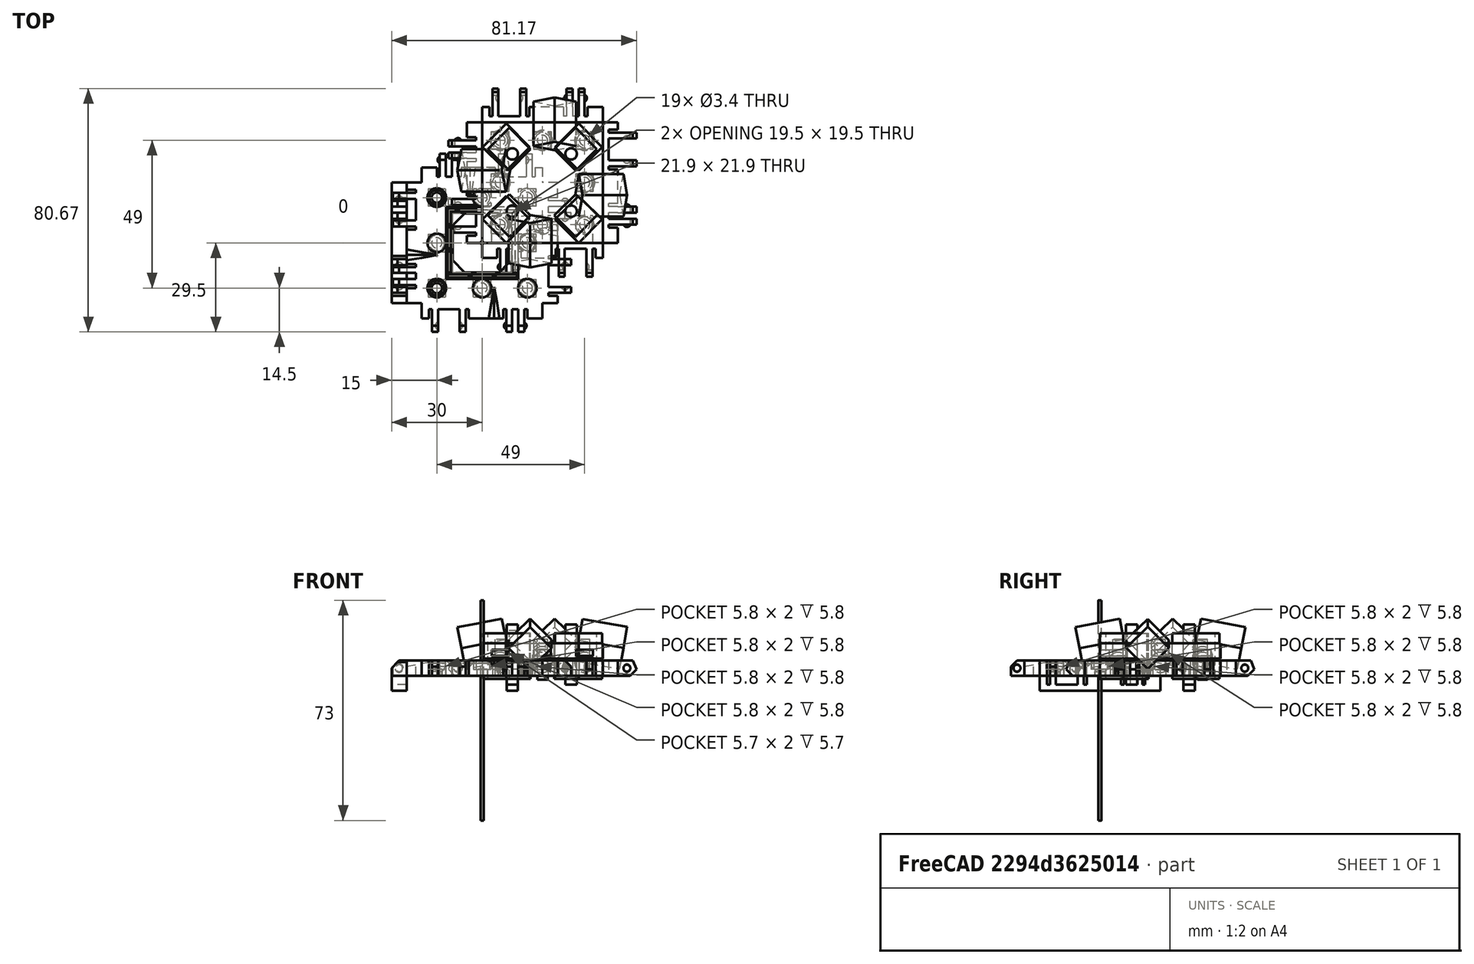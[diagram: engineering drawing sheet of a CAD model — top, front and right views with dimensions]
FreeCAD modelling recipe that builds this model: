
FCSTD DOCUMENT  (FreeCAD 0.17R13522 (Git))
Label: Robot Plates 1.0
License: All rights reserved
LicenseURL: http://en.wikipedia.org/wiki/All_rights_reserved
objects: Part::Box×265, Part::Cut×89, Part::Sphere×84, Part::MultiFuse×63, Part::Fuse×30, Part::Cylinder×29, Part::Chamfer×11, Drawing::FeatureViewAnnotation×6, App::DocumentObjectGroup×3, Part::Feature×3, Drawing::FeaturePage×2
note: 574 computed .brp shape members not serialized (recipe doc carries the construction recipe); baked Part::Feature solids carry a one-line shape summary decoded from their .brp

FEATURE [Part::Box] Box  label="Cube"
  AttacherType = Attacher::AttachEngine3D
  Height = 5
  Length = 40
  Placement = pos=(-20,-20,-2) rot=(0,0,1;0rad)
  Width = 40
FEATURE [Part::Sphere] Sphere003  label="Mag Hole 3"
  Angle1 = -90
  Angle2 = 90
  Angle3 = 360
  AttacherType = Attacher::AttachEngine3D
  Placement = pos=(-15,15,1.7) rot=(0,0,1;0rad)
  Radius = 2.85
FEATURE [Part::Sphere] Sphere005  label="Mag Hole 2"
  Angle1 = -90
  Angle2 = 90
  Angle3 = 360
  AttacherType = Attacher::AttachEngine3D
  Placement = pos=(15,0,1.7) rot=(0,0,1;0rad)
  Radius = 2.85
FEATURE [Part::Sphere] Sphere  label="Mag Hole"
  Angle1 = -90
  Angle2 = 90
  Angle3 = 360
  AttacherType = Attacher::AttachEngine3D
  Placement = pos=(-15,-15,1.7) rot=(0,0,1;0rad)
  Radius = 2.85
FEATURE [Part::MultiFuse] Fusion004  label="Ball Holes"
  Shapes = -> [Sphere,Sphere005,Sphere003]
FEATURE [Part::Cut] Cut003
  Base = -> Box
  Tool = -> Fusion004
FEATURE [Part::Box] Box001  label="Cube001"
  AttacherType = Attacher::AttachEngine3D
  Height = 7
  Length = 5
  Placement = pos=(-5,0,-2) rot=(0,0,1;0rad)
  Width = 40
FEATURE [Part::Box] Box002  label="Cube002"
  AttacherType = Attacher::AttachEngine3D
  Height = 7
  Length = 10
  Placement = pos=(-15,6,-2) rot=(0,0,1;0rad)
  Width = 2
FEATURE [Part::Box] Box003  label="Cube003"
  AttacherType = Attacher::AttachEngine3D
  Height = 7
  Length = 10
  Placement = pos=(-15,10,-2) rot=(0,0,1;0rad)
  Width = 2
FEATURE [Part::Box] Box004  label="Cube004"
  AttacherType = Attacher::AttachEngine3D
  Height = 7
  Length = 10
  Placement = pos=(-15,25.4,-2) rot=(0,0,1;0rad)
  Width = 2
FEATURE [Part::Box] Box005  label="Cube005"
  AttacherType = Attacher::AttachEngine3D
  Height = 7
  Length = 10
  Placement = pos=(-15,34.6,-2) rot=(0,0,1;0rad)
  Width = 2
FEATURE [Part::Sphere] Sphere008
  Angle1 = -90
  Angle2 = 90
  Angle3 = 360
  AttacherType = Attacher::AttachEngine3D
  Placement = pos=(-7.5,6.5,0.5) rot=(0,0,1;0rad)
  Radius = 1.25
FEATURE [Part::Box] Box006  label="Chamfer Cube"
  AttacherType = Attacher::AttachEngine3D
  Height = 10
  Length = 13
  Placement = pos=(-11.69,0,-1.19) rot=(0,-1,0;0.785398rad)
  Width = 40
FEATURE [Part::Sphere] Sphere009
  Angle1 = -90
  Angle2 = 90
  Angle3 = 360
  AttacherType = Attacher::AttachEngine3D
  Placement = pos=(-7.5,11.5,0.5) rot=(0,0,1;0rad)
  Radius = 1.25
FEATURE [Part::Sphere] Sphere010
  Angle1 = -90
  Angle2 = 90
  Angle3 = 360
  AttacherType = Attacher::AttachEngine3D
  Placement = pos=(-7.5,28,0.5) rot=(0,0,1;0rad)
  Radius = 1.5
FEATURE [Part::Sphere] Sphere011
  Angle1 = -90
  Angle2 = 90
  Angle3 = 360
  AttacherType = Attacher::AttachEngine3D
  Placement = pos=(-7.5,34,0.5) rot=(0,0,1;0rad)
  Radius = 1.5
FEATURE [Part::Box] Box007  label="Cube007"
  AttacherType = Attacher::AttachEngine3D
  Height = 7
  Length = 4
  Placement = pos=(-6,5,-2) rot=(0,0,1;0rad)
  Width = 1
FEATURE [Part::Box] Box008  label="Cube008"
  AttacherType = Attacher::AttachEngine3D
  Height = 7
  Length = 4
  Placement = pos=(-6,8,-2) rot=(0,0,1;0rad)
  Width = 2
FEATURE [Part::Box] Box009  label="Cube009"
  AttacherType = Attacher::AttachEngine3D
  Height = 7
  Length = 4
  Placement = pos=(-6,12,-2) rot=(0,0,1;0rad)
  Width = 1
FEATURE [Part::Box] Box010  label="Cube010"
  AttacherType = Attacher::AttachEngine3D
  Height = 7
  Length = 4
  Placement = pos=(-6,24.4,-2) rot=(0,0,1;0rad)
  Width = 1
FEATURE [Part::Box] Box011  label="Cube011"
  AttacherType = Attacher::AttachEngine3D
  Height = 7
  Length = 4
  Placement = pos=(-6,36.6,-2) rot=(0,0,1;0rad)
  Width = 1
FEATURE [Part::Box] Box012  label="Cube012"
  AttacherType = Attacher::AttachEngine3D
  Height = 7
  Length = 4
  Placement = pos=(-6,27.4,-2) rot=(0,0,1;0rad)
  Width = 7.2
FEATURE [Part::MultiFuse] Fusion003  label="Extra Holes for Clips"
  Shapes = -> [Box012,Box009,Box011,Box008,Box010,Box007]
FEATURE [Part::Box] Box013  label="Re-level Edge Clip Block"
  AttacherType = Attacher::AttachEngine3D
  Height = 10
  Length = 20
  Placement = pos=(-19,-2,3) rot=(0,0,1;0rad)
  Width = 44
FEATURE [Part::Box] Box014  label="Cube014"
  AttacherType = Attacher::AttachEngine3D
  Height = 7
  Length = 10
  Placement = pos=(-10,34.6,0) rot=(0,0,1;0rad)
  Width = 2
FEATURE [Part::Box] Box015  label="Cube015"
  AttacherType = Attacher::AttachEngine3D
  Height = 7
  Length = 5
  Width = 40
FEATURE [Part::Box] Box016  label="Cube016"
  AttacherType = Attacher::AttachEngine3D
  Height = 7
  Length = 10
  Placement = pos=(-10,25.4,0) rot=(0,0,1;0rad)
  Width = 2
FEATURE [Part::Box] Box017  label="Cube017"
  AttacherType = Attacher::AttachEngine3D
  Height = 7
  Length = 10
  Placement = pos=(-10,10,0) rot=(0,0,1;0rad)
  Width = 2
FEATURE [Part::Box] Box018  label="Cube018"
  AttacherType = Attacher::AttachEngine3D
  Height = 7
  Length = 10
  Placement = pos=(-10,6,0) rot=(0,0,1;0rad)
  Width = 2
FEATURE [Part::Sphere] Sphere012
  Angle1 = -90
  Angle2 = 90
  Angle3 = 360
  AttacherType = Attacher::AttachEngine3D
  Placement = pos=(-3,6.5,2.5) rot=(0,0,1;0rad)
  Radius = 1.25
FEATURE [Part::Box] Box019  label="Cube019"
  AttacherType = Attacher::AttachEngine3D
  Height = 10
  Length = 13
  Placement = pos=(-10.19,0,-1.19) rot=(0,-1,0;0.785398rad)
  Width = 40
FEATURE [Part::Sphere] Sphere013
  Angle1 = -90
  Angle2 = 90
  Angle3 = 360
  AttacherType = Attacher::AttachEngine3D
  Placement = pos=(-3,11.5,2.5) rot=(0,0,1;0rad)
  Radius = 1.25
FEATURE [Part::Sphere] Sphere014
  Angle1 = -90
  Angle2 = 90
  Angle3 = 360
  AttacherType = Attacher::AttachEngine3D
  Placement = pos=(-3,28,2.5) rot=(0,0,1;0rad)
  Radius = 1.5
FEATURE [Part::Sphere] Sphere015
  Angle1 = -90
  Angle2 = 90
  Angle3 = 360
  AttacherType = Attacher::AttachEngine3D
  Placement = pos=(-3,34,2.5) rot=(0,0,1;0rad)
  Radius = 1.5
FEATURE [Part::MultiFuse] Fusion005
  Shapes = -> [Box015,Box018,Box017,Box016,Box014]
FEATURE [Part::Cut] Cut005
  Base = -> Fusion005
  Tool = -> Box019
FEATURE [Part::MultiFuse] Fusion006
  Shapes = -> [Sphere012,Sphere013,Cut005]
FEATURE [Part::MultiFuse] Fusion007
  Shapes = -> [Sphere015,Sphere014]
FEATURE [Part::Cut] Cut006
  Base = -> Fusion006
  Tool = -> Fusion007
FEATURE [Part::Chamfer] Chamfer002
  Base = -> Cut006
  Edges = 4 edges r=4: [Edge31,Edge37,Edge43,Edge46]
FEATURE [Part::Box] Box020  label="Cube020"
  AttacherType = Attacher::AttachEngine3D
  Height = 7
  Length = 4
  Placement = pos=(-1,5,0) rot=(0,0,1;0rad)
  Width = 1
FEATURE [Part::Box] Box021  label="Cube021"
  AttacherType = Attacher::AttachEngine3D
  Height = 7
  Length = 4
  Placement = pos=(-1,8,0) rot=(0,0,1;0rad)
  Width = 2
FEATURE [Part::Box] Box022  label="Cube022"
  AttacherType = Attacher::AttachEngine3D
  Height = 7
  Length = 4
  Placement = pos=(-1,12,0) rot=(0,0,1;0rad)
  Width = 1
FEATURE [Part::Box] Box023  label="Cube023"
  AttacherType = Attacher::AttachEngine3D
  Height = 7
  Length = 4
  Placement = pos=(-1,24.4,0) rot=(0,0,1;0rad)
  Width = 1
FEATURE [Part::Box] Box024  label="Cube024"
  AttacherType = Attacher::AttachEngine3D
  Height = 7
  Length = 4
  Placement = pos=(-1,36.6,0) rot=(0,0,1;0rad)
  Width = 1
FEATURE [Part::Box] Box025  label="Cube025"
  AttacherType = Attacher::AttachEngine3D
  Height = 7
  Length = 4
  Placement = pos=(-1,27.4,0) rot=(0,0,1;0rad)
  Width = 7.2
FEATURE [Part::MultiFuse] Fusion008
  Shapes = -> [Box025,Box022,Box024,Box021,Box023,Box020]
FEATURE [Part::Cut] Cut007
  Base = -> Chamfer002
  Placement = pos=(-5,40,3) rot=(1,0,0;3.14159rad)
  Tool = -> Fusion008
FEATURE [Part::Box] Box026  label="Cube026"
  AttacherType = Attacher::AttachEngine3D
  Height = 10
  Length = 12
  Placement = pos=(-11,-2,-12) rot=(0,0,1;0rad)
  Width = 44
FEATURE [Part::Cut] Cut008
  Base = -> Cut007
  Placement = pos=(40,0,0) rot=(0,0,1;1.5708rad)
  Tool = -> Box026
FEATURE [Part::Box] Box027  label="Cube027"
  AttacherType = Attacher::AttachEngine3D
  Height = 7
  Length = 4
  Placement = pos=(-1,12,0) rot=(0,0,1;0rad)
  Width = 1
FEATURE [Part::Box] Box028  label="Cube028"
  AttacherType = Attacher::AttachEngine3D
  Height = 10
  Length = 13
  Placement = pos=(-10.19,0,-1.19) rot=(0,-1,0;0.785398rad)
  Width = 40
FEATURE [Part::Box] Box029  label="Cube029"
  AttacherType = Attacher::AttachEngine3D
  Height = 7
  Length = 4
  Placement = pos=(-1,27.4,0) rot=(0,0,1;0rad)
  Width = 7.2
FEATURE [Part::Box] Box030  label="Cube030"
  AttacherType = Attacher::AttachEngine3D
  Height = 7
  Length = 4
  Placement = pos=(-1,5,0) rot=(0,0,1;0rad)
  Width = 1
FEATURE [Part::Box] Box031  label="Cube031"
  AttacherType = Attacher::AttachEngine3D
  Height = 7
  Length = 10
  Placement = pos=(-10,6,0) rot=(0,0,1;0rad)
  Width = 2
FEATURE [Part::Box] Box032  label="Cube032"
  AttacherType = Attacher::AttachEngine3D
  Height = 10
  Length = 12
  Placement = pos=(-11,-2,-12) rot=(0,0,1;0rad)
  Width = 44
FEATURE [Part::Sphere] Sphere016
  Angle1 = -90
  Angle2 = 90
  Angle3 = 360
  AttacherType = Attacher::AttachEngine3D
  Placement = pos=(-3,6.5,2.5) rot=(0,0,1;0rad)
  Radius = 1.25
FEATURE [Part::Box] Box033  label="Cube033"
  AttacherType = Attacher::AttachEngine3D
  Height = 7
  Length = 10
  Placement = pos=(-10,25.4,0) rot=(0,0,1;0rad)
  Width = 2
FEATURE [Part::Box] Box034  label="Cube034"
  AttacherType = Attacher::AttachEngine3D
  Height = 7
  Length = 10
  Placement = pos=(-10,10,0) rot=(0,0,1;0rad)
  Width = 2
FEATURE [Part::Sphere] Sphere017
  Angle1 = -90
  Angle2 = 90
  Angle3 = 360
  AttacherType = Attacher::AttachEngine3D
  Placement = pos=(-3,28,2.5) rot=(0,0,1;0rad)
  Radius = 1.5
FEATURE [Part::Sphere] Sphere018
  Angle1 = -90
  Angle2 = 90
  Angle3 = 360
  AttacherType = Attacher::AttachEngine3D
  Placement = pos=(-3,11.5,2.5) rot=(0,0,1;0rad)
  Radius = 1.25
FEATURE [Part::Box] Box035  label="Cube035"
  AttacherType = Attacher::AttachEngine3D
  Height = 7
  Length = 4
  Placement = pos=(-1,36.6,0) rot=(0,0,1;0rad)
  Width = 1
FEATURE [Part::Sphere] Sphere019
  Angle1 = -90
  Angle2 = 90
  Angle3 = 360
  AttacherType = Attacher::AttachEngine3D
  Placement = pos=(-3,34,2.5) rot=(0,0,1;0rad)
  Radius = 1.5
FEATURE [Part::MultiFuse] Fusion011
  Shapes = -> [Sphere019,Sphere017]
FEATURE [Part::Box] Box036  label="Cube036"
  AttacherType = Attacher::AttachEngine3D
  Height = 7
  Length = 4
  Placement = pos=(-1,8,0) rot=(0,0,1;0rad)
  Width = 2
FEATURE [Part::Box] Box037  label="Cube037"
  AttacherType = Attacher::AttachEngine3D
  Height = 7
  Length = 10
  Placement = pos=(-10,34.6,0) rot=(0,0,1;0rad)
  Width = 2
FEATURE [Part::Box] Box038  label="Cube038"
  AttacherType = Attacher::AttachEngine3D
  Height = 7
  Length = 4
  Placement = pos=(-1,24.4,0) rot=(0,0,1;0rad)
  Width = 1
FEATURE [Part::MultiFuse] Fusion009
  Shapes = -> [Box029,Box027,Box035,Box036,Box038,Box030]
FEATURE [Part::Box] Box039  label="Cube039"
  AttacherType = Attacher::AttachEngine3D
  Height = 7
  Length = 5
  Width = 40
FEATURE [Part::MultiFuse] Fusion012
  Shapes = -> [Box039,Box031,Box034,Box033,Box037]
FEATURE [Part::Cut] Cut011
  Base = -> Fusion012
  Tool = -> Box028
FEATURE [Part::MultiFuse] Fusion010
  Shapes = -> [Sphere016,Sphere018,Cut011]
FEATURE [Part::Cut] Cut012
  Base = -> Fusion010
  Tool = -> Fusion011
FEATURE [Part::Chamfer] Chamfer003
  Base = -> Cut012
  Edges = 4 edges r=4: [Edge31,Edge37,Edge43,Edge46]
FEATURE [Part::Cut] Cut010
  Base = -> Chamfer003
  Placement = pos=(-5,40,3) rot=(1,0,0;3.14159rad)
  Tool = -> Fusion009
FEATURE [Part::Cut] Cut009
  Base = -> Cut010
  Placement = pos=(40,40,0) rot=(0,0,1;3.14159rad)
  Tool = -> Box032
FEATURE [Part::Sphere] Sphere020
  Angle1 = -90
  Angle2 = 90
  Angle3 = 360
  AttacherType = Attacher::AttachEngine3D
  Placement = pos=(-3,11.5,2.5) rot=(0,0,1;0rad)
  Radius = 1.25
FEATURE [Part::Box] Box040  label="Cube040"
  AttacherType = Attacher::AttachEngine3D
  Height = 7
  Length = 10
  Placement = pos=(-10,6,0) rot=(0,0,1;0rad)
  Width = 2
FEATURE [Part::Box] Box041  label="Cube041"
  AttacherType = Attacher::AttachEngine3D
  Height = 7
  Length = 4
  Placement = pos=(-1,8,0) rot=(0,0,1;0rad)
  Width = 2
FEATURE [Part::Box] Box042  label="Cube042"
  AttacherType = Attacher::AttachEngine3D
  Height = 7
  Length = 10
  Placement = pos=(-10,10,0) rot=(0,0,1;0rad)
  Width = 2
FEATURE [Part::Box] Box043  label="Cube043"
  AttacherType = Attacher::AttachEngine3D
  Height = 10
  Length = 12
  Placement = pos=(-11,-2,-12) rot=(0,0,1;0rad)
  Width = 44
FEATURE [Part::Box] Box044  label="Cube044"
  AttacherType = Attacher::AttachEngine3D
  Height = 7
  Length = 4
  Placement = pos=(-1,5,0) rot=(0,0,1;0rad)
  Width = 1
FEATURE [Part::Sphere] Sphere021
  Angle1 = -90
  Angle2 = 90
  Angle3 = 360
  AttacherType = Attacher::AttachEngine3D
  Placement = pos=(-3,28,2.5) rot=(0,0,1;0rad)
  Radius = 1.5
FEATURE [Part::Sphere] Sphere022
  Angle1 = -90
  Angle2 = 90
  Angle3 = 360
  AttacherType = Attacher::AttachEngine3D
  Placement = pos=(-3,6.5,2.5) rot=(0,0,1;0rad)
  Radius = 1.25
FEATURE [Part::Sphere] Sphere023
  Angle1 = -90
  Angle2 = 90
  Angle3 = 360
  AttacherType = Attacher::AttachEngine3D
  Placement = pos=(-3,34,2.5) rot=(0,0,1;0rad)
  Radius = 1.5
FEATURE [Part::Box] Box045  label="Cube045"
  AttacherType = Attacher::AttachEngine3D
  Height = 7
  Length = 4
  Placement = pos=(-1,12,0) rot=(0,0,1;0rad)
  Width = 1
FEATURE [Part::Box] Box046  label="Cube046"
  AttacherType = Attacher::AttachEngine3D
  Height = 7
  Length = 5
  Width = 40
FEATURE [Part::Box] Box047  label="Cube047"
  AttacherType = Attacher::AttachEngine3D
  Height = 7
  Length = 4
  Placement = pos=(-1,36.6,0) rot=(0,0,1;0rad)
  Width = 1
FEATURE [Part::Box] Box048  label="Cube048"
  AttacherType = Attacher::AttachEngine3D
  Height = 7
  Length = 4
  Placement = pos=(-1,24.4,0) rot=(0,0,1;0rad)
  Width = 1
FEATURE [Part::Box] Box049  label="Cube049"
  AttacherType = Attacher::AttachEngine3D
  Height = 7
  Length = 10
  Placement = pos=(-10,25.4,0) rot=(0,0,1;0rad)
  Width = 2
FEATURE [Part::Box] Box050  label="Cube050"
  AttacherType = Attacher::AttachEngine3D
  Height = 10
  Length = 13
  Placement = pos=(-10.19,0,-1.19) rot=(0,-1,0;0.785398rad)
  Width = 40
FEATURE [Part::Box] Box051  label="Cube051"
  AttacherType = Attacher::AttachEngine3D
  Height = 7
  Length = 10
  Placement = pos=(-10,34.6,0) rot=(0,0,1;0rad)
  Width = 2
FEATURE [Part::MultiFuse] Fusion015
  Shapes = -> [Box046,Box040,Box042,Box049,Box051]
FEATURE [Part::Cut] Cut013
  Base = -> Fusion015
  Tool = -> Box050
FEATURE [Part::MultiFuse] Fusion013
  Shapes = -> [Sphere022,Sphere020,Cut013]
FEATURE [Part::MultiFuse] Fusion016
  Shapes = -> [Sphere023,Sphere021]
FEATURE [Part::Cut] Cut014
  Base = -> Fusion013
  Tool = -> Fusion016
FEATURE [Part::Chamfer] Chamfer004
  Base = -> Cut014
  Edges = 4 edges r=4: [Edge31,Edge37,Edge43,Edge46]
FEATURE [Part::Box] Box052  label="Cube052"
  AttacherType = Attacher::AttachEngine3D
  Height = 7
  Length = 4
  Placement = pos=(-1,27.4,0) rot=(0,0,1;0rad)
  Width = 7.2
FEATURE [Part::MultiFuse] Fusion014
  Shapes = -> [Box052,Box045,Box047,Box041,Box048,Box044]
FEATURE [Part::Cut] Cut016
  Base = -> Chamfer004
  Placement = pos=(-5,40,3) rot=(1,0,0;3.14159rad)
  Tool = -> Fusion014
FEATURE [Part::Cut] Cut015
  Base = -> Cut016
  Placement = pos=(0,40,0) rot=(0,0,-1;1.5708rad)
  Tool = -> Box043
FEATURE [Part::Box] Box054  label="Cube054"
  AttacherType = Attacher::AttachEngine3D
  Height = 15
  Length = 10
  Placement = pos=(9,2,-3) rot=(0,0,1;0.785398rad)
  Width = 10
FEATURE [Part::Box] Box055  label="Cube055"
  AttacherType = Attacher::AttachEngine3D
  Height = 15
  Length = 10
  Placement = pos=(31,24,-3) rot=(0,0,1;0.785398rad)
  Width = 10
FEATURE [Part::Box] Box056  label="Cube056"
  AttacherType = Attacher::AttachEngine3D
  Height = 15
  Length = 10
  Placement = pos=(31,2,-3) rot=(0,0,1;0.785398rad)
  Width = 10
FEATURE [Part::Box] Box057  label="Cube057"
  AttacherType = Attacher::AttachEngine3D
  Height = 15
  Length = 10
  Placement = pos=(9,24,-3) rot=(0,0,1;0.785398rad)
  Width = 10
FEATURE [Part::MultiFuse] Fusion017
  Shapes = -> [Box054,Box057,Box056,Box055]
FEATURE [Part::Box] Box058  label="Cube058"
  AttacherType = Attacher::AttachEngine3D
  Height = 5
  Length = 40
  Placement = pos=(0,0,3.7) rot=(0,0,1;0rad)
  Width = 40
FEATURE [Part::Box] Box059  label="Square Nut Hole 008"
  AttacherType = Attacher::AttachEngine3D
  Height = 2
  Length = 5.6
  Placement = pos=(17.2,31.2,4.6) rot=(0,0,1;0rad)
  Width = 5.6
FEATURE [Part::Box] Box060  label="Square Nut Hole 009"
  AttacherType = Attacher::AttachEngine3D
  Height = 2
  Length = 5.6
  Placement = pos=(17.2,-0.85,4.6) rot=(0,0,1;0rad)
  Width = 10
FEATURE [Part::Box] Box061  label="Square Nut Hole 010"
  AttacherType = Attacher::AttachEngine3D
  Height = 2
  Length = 5.6
  Placement = pos=(31.2,-0.85,4.6) rot=(0,0,1;0rad)
  Width = 10
FEATURE [Part::Box] Box062  label="Square Nut Hole 011"
  AttacherType = Attacher::AttachEngine3D
  Height = 2
  Length = 5.4
  Placement = pos=(31.3,17.3,4.6) rot=(0,0,1;0rad)
  Width = 5.4
FEATURE [Part::Box] Box063  label="Square Nut Hole 012"
  AttacherType = Attacher::AttachEngine3D
  Height = 2
  Length = 5.7
  Placement = pos=(3.15,31.15,4.6) rot=(0,0,1;0rad)
  Width = 5.7
FEATURE [Part::Box] Box064  label="Square Nut Hole 013"
  AttacherType = Attacher::AttachEngine3D
  Height = 2
  Length = 5.5
  Placement = pos=(31.25,31.25,4.6) rot=(0,0,1;0rad)
  Width = 5.5
FEATURE [Part::Box] Box065  label="Square Nut Hole 014"
  AttacherType = Attacher::AttachEngine3D
  Height = 2
  Length = 5.8
  Placement = pos=(3.1,17.1,4.6) rot=(0,0,1;0rad)
  Width = 5.8
FEATURE [Part::Box] Box066  label="Square Nut Hole 015"
  AttacherType = Attacher::AttachEngine3D
  Height = 2
  Length = 5.6
  Placement = pos=(3.2,-0.85,4.6) rot=(0,0,1;0rad)
  Width = 10
FEATURE [Part::Sphere] Sphere006  label="Nut Clearence1"
  Angle1 = -90
  Angle2 = 90
  Angle3 = 360
  AttacherType = Attacher::AttachEngine3D
  Placement = pos=(6,6,2.4) rot=(0,0,1;0rad)
  Radius = 3.35
FEATURE [Part::Sphere] Sphere024
  Angle1 = -90
  Angle2 = 90
  Angle3 = 360
  AttacherType = Attacher::AttachEngine3D
  Placement = pos=(6,34,2.4) rot=(0,0,1;0rad)
  Radius = 3.35
FEATURE [Part::Sphere] Sphere007
  Angle1 = -90
  Angle2 = 90
  Angle3 = 360
  AttacherType = Attacher::AttachEngine3D
  Placement = pos=(34,20,2.4) rot=(0,0,1;0rad)
  Radius = 3.35
FEATURE [Part::Sphere] Sphere001
  Angle1 = -90
  Angle2 = 90
  Angle3 = 360
  AttacherType = Attacher::AttachEngine3D
  Placement = pos=(34,6,2.4) rot=(0,0,1;0rad)
  Radius = 3.35
FEATURE [Part::Sphere] Sphere025
  Angle1 = -90
  Angle2 = 90
  Angle3 = 360
  AttacherType = Attacher::AttachEngine3D
  Placement = pos=(20,6,2.4) rot=(0,0,1;0rad)
  Radius = 3.35
FEATURE [Part::Sphere] Sphere026
  Angle1 = -90
  Angle2 = 90
  Angle3 = 360
  AttacherType = Attacher::AttachEngine3D
  Placement = pos=(20,34,2.4) rot=(0,0,1;0rad)
  Radius = 3.35
FEATURE [Part::Sphere] Sphere004
  Angle1 = -90
  Angle2 = 90
  Angle3 = 360
  AttacherType = Attacher::AttachEngine3D
  Placement = pos=(6,20,2.4) rot=(0,0,1;0rad)
  Radius = 3.35
FEATURE [Part::Sphere] Sphere002
  Angle1 = -90
  Angle2 = 90
  Angle3 = 360
  AttacherType = Attacher::AttachEngine3D
  Placement = pos=(34,34,2.4) rot=(0,0,1;0rad)
  Radius = 3.35
FEATURE [Part::Cylinder] Cylinder
  Angle = 360
  AttacherType = Attacher::AttachEngine3D
  Height = 10
  Placement = pos=(6,6,0) rot=(0,0,1;0rad)
  Radius = 1.7
FEATURE [Part::Cylinder] Cylinder002
  Angle = 360
  AttacherType = Attacher::AttachEngine3D
  Height = 10
  Placement = pos=(34,6,0) rot=(0,0,1;0rad)
  Radius = 1.7
FEATURE [Part::Cylinder] Cylinder001
  Angle = 360
  AttacherType = Attacher::AttachEngine3D
  Height = 10
  Placement = pos=(20,6,0) rot=(0,0,1;0rad)
  Radius = 1.7
FEATURE [Part::Cylinder] Cylinder003
  Angle = 360
  AttacherType = Attacher::AttachEngine3D
  Height = 10
  Placement = pos=(34,34,0) rot=(0,0,1;0rad)
  Radius = 1.7
FEATURE [Part::Cylinder] Cylinder004
  Angle = 360
  AttacherType = Attacher::AttachEngine3D
  Height = 10
  Placement = pos=(20,34,0) rot=(0,0,1;0rad)
  Radius = 1.7
FEATURE [Part::Cylinder] Cylinder005
  Angle = 360
  AttacherType = Attacher::AttachEngine3D
  Height = 10
  Placement = pos=(6,34,0) rot=(0,0,1;0rad)
  Radius = 1.7
FEATURE [Part::Cylinder] Cylinder006
  Angle = 360
  AttacherType = Attacher::AttachEngine3D
  Height = 10
  Placement = pos=(6,20,0) rot=(0,0,1;0rad)
  Radius = 1.7
FEATURE [Part::Cylinder] Cylinder007
  Angle = 360
  AttacherType = Attacher::AttachEngine3D
  Height = 10
  Placement = pos=(34,20,0) rot=(0,0,1;0rad)
  Radius = 1.7
FEATURE [Part::MultiFuse] Fusion018
  Shapes = -> [Cylinder,Cylinder004,Cylinder007,Cylinder005,Cylinder006,Cylinder001,Cylinder002,Cylinder003]
FEATURE [Part::MultiFuse] Fusion019
  Shapes = -> [Sphere007,Sphere024,Sphere006,Sphere025,Sphere001,Sphere026,Sphere004,Sphere002]
FEATURE [Part::MultiFuse] Fusion020
  Shapes = -> [Box061,Box065,Box062,Box063,Box064,Box066,Box059,Box060]
FEATURE [Part::Cut] Cut017
  Base = -> Box058
  Tool = -> Fusion020
FEATURE [Part::Cut] Cut019
  Base = -> Cut017
  Tool = -> Fusion019
FEATURE [Part::Cut] Cut018
  Base = -> Cut019
  Tool = -> Fusion018
FEATURE [Part::Cylinder] Cylinder008
  Angle = 360
  AttacherType = Attacher::AttachEngine3D
  Height = 20
  Placement = pos=(10,10.5,-5) rot=(0,0,1;0rad)
  Radius = 1.9
FEATURE [Part::Cylinder] Cylinder009
  Angle = 360
  AttacherType = Attacher::AttachEngine3D
  Height = 20
  Placement = pos=(29.5,10.5,-5) rot=(0,0,1;0rad)
  Radius = 1.9
FEATURE [Part::Cylinder] Cylinder010
  Angle = 360
  AttacherType = Attacher::AttachEngine3D
  Height = 20
  Placement = pos=(29.5,29.5,-5) rot=(0,0,1;0rad)
  Radius = 1.9
FEATURE [Part::Cylinder] Cylinder011
  Angle = 360
  AttacherType = Attacher::AttachEngine3D
  Height = 20
  Placement = pos=(10,29.5,-7) rot=(0,0,1;0rad)
  Radius = 1.9
FEATURE [Part::MultiFuse] Fusion021  label="M2 Screw holes"
  Shapes = -> [Cylinder008,Cylinder009,Cylinder011,Cylinder010]
FEATURE [Part::Box] Box067  label="Square Nut Hole 016"
  AttacherType = Attacher::AttachEngine3D
  Height = 2
  Length = 5.8
  Placement = pos=(31.1,17.1,4.6) rot=(0,0,1;0rad)
  Width = 5.8
FEATURE [Part::Box] Box068  label="Square Nut Hole 017"
  AttacherType = Attacher::AttachEngine3D
  Height = 2
  Length = 5.8
  Placement = pos=(17.1,36.9,2.1) rot=(1,0,0;3.14159rad)
  Width = 5.8
FEATURE [Part::Box] Box069  label="Square Nut Hole 018"
  AttacherType = Attacher::AttachEngine3D
  Height = 2
  Length = 5.8
  Placement = pos=(-2.9,2.9,2.1) rot=(1,0,0;3.14159rad)
  Width = 5.8
FEATURE [Part::Box] Box070  label="Square Nut Hole 019"
  AttacherType = Attacher::AttachEngine3D
  Height = 2
  Length = 5.8
  Placement = pos=(3.1,3.1,4.6) rot=(0,0,1;0rad)
  Width = 5.8
FEATURE [Part::Box] Box071  label="Square Nut Hole 020"
  AttacherType = Attacher::AttachEngine3D
  Height = 2
  Length = 5.8
  Placement = pos=(3.1,31.1,4.6) rot=(0,0,1;0rad)
  Width = 5.8
FEATURE [Part::Box] Box072  label="Square Nut Hole 021"
  AttacherType = Attacher::AttachEngine3D
  Height = 2
  Length = 5.8
  Placement = pos=(17.1,31.1,4.6) rot=(0,0,1;0rad)
  Width = 5.8
FEATURE [Part::Box] Box073  label="Square Nut Hole 022"
  AttacherType = Attacher::AttachEngine3D
  Height = 2
  Length = 5.8
  Placement = pos=(31.1,31.1,4.6) rot=(0,0,1;0rad)
  Width = 5.8
FEATURE [Part::Box] Box074  label="Square Nut Hole 023"
  AttacherType = Attacher::AttachEngine3D
  Height = 2
  Length = 5.8
  Placement = pos=(3.1,17.1,4.6) rot=(0,0,1;0rad)
  Width = 5.8
FEATURE [Part::Cylinder] Cylinder012
  Angle = 360
  AttacherType = Attacher::AttachEngine3D
  Height = 10
  Placement = pos=(6,6,0) rot=(0,0,1;0rad)
  Radius = 1.7
FEATURE [Part::Cylinder] Cylinder013
  Angle = 360
  AttacherType = Attacher::AttachEngine3D
  Height = 10
  Placement = pos=(34,34,0) rot=(0,0,1;0rad)
  Radius = 1.7
FEATURE [Part::Cylinder] Cylinder014
  Angle = 360
  AttacherType = Attacher::AttachEngine3D
  Height = 10
  Placement = pos=(20,34,0) rot=(0,0,1;0rad)
  Radius = 1.7
FEATURE [Part::Cylinder] Cylinder015
  Angle = 360
  AttacherType = Attacher::AttachEngine3D
  Height = 10
  Placement = pos=(6,34,0) rot=(0,0,1;0rad)
  Radius = 1.7
FEATURE [Part::Cylinder] Cylinder016
  Angle = 360
  AttacherType = Attacher::AttachEngine3D
  Height = 10
  Placement = pos=(6,20,0) rot=(0,0,1;0rad)
  Radius = 1.7
FEATURE [Part::Cylinder] Cylinder017
  Angle = 360
  AttacherType = Attacher::AttachEngine3D
  Height = 10
  Placement = pos=(34,20,0) rot=(0,0,1;0rad)
  Radius = 1.7
FEATURE [Part::Cylinder] Cylinder018
  Angle = 360
  AttacherType = Attacher::AttachEngine3D
  Height = 10
  Placement = pos=(0,0,6.7) rot=(1,0,0;3.14159rad)
  Radius = 1.7
FEATURE [Part::Cylinder] Cylinder019
  Angle = 360
  AttacherType = Attacher::AttachEngine3D
  Height = 10
  Placement = pos=(20,34,6.7) rot=(1,0,0;3.14159rad)
  Radius = 1.7
FEATURE [Part::Box] Box075  label="Cube059"
  AttacherType = Attacher::AttachEngine3D
  Height = 5
  Length = 40
  Placement = pos=(-20,-20,-2) rot=(0,0,1;0rad)
  Width = 40
FEATURE [Part::Sphere] Sphere027
  Angle1 = -90
  Angle2 = 90
  Angle3 = 360
  AttacherType = Attacher::AttachEngine3D
  Placement = pos=(34,20,2.4) rot=(0,0,1;0rad)
  Radius = 3.35
FEATURE [Part::Sphere] Sphere028  label="Nut Clearence002"
  Angle1 = -90
  Angle2 = 90
  Angle3 = 360
  AttacherType = Attacher::AttachEngine3D
  Placement = pos=(6,6,2.4) rot=(0,0,1;0rad)
  Radius = 3.35
FEATURE [Part::Sphere] Sphere029
  Angle1 = -90
  Angle2 = 90
  Angle3 = 360
  AttacherType = Attacher::AttachEngine3D
  Placement = pos=(34,34,2.4) rot=(0,0,1;0rad)
  Radius = 3.35
FEATURE [Part::Sphere] Sphere030
  Angle1 = -90
  Angle2 = 90
  Angle3 = 360
  AttacherType = Attacher::AttachEngine3D
  Placement = pos=(0,0,4.3) rot=(1,0,0;3.14159rad)
  Radius = 3.35
FEATURE [Part::Sphere] Sphere031
  Angle1 = -90
  Angle2 = 90
  Angle3 = 360
  AttacherType = Attacher::AttachEngine3D
  Placement = pos=(20,34,4.3) rot=(1,0,0;3.14159rad)
  Radius = 3.35
FEATURE [Part::Sphere] Sphere032
  Angle1 = -90
  Angle2 = 90
  Angle3 = 360
  AttacherType = Attacher::AttachEngine3D
  Placement = pos=(6,34,2.4) rot=(0,0,1;0rad)
  Radius = 3.35
FEATURE [Part::Sphere] Sphere033
  Angle1 = -90
  Angle2 = 90
  Angle3 = 360
  AttacherType = Attacher::AttachEngine3D
  Placement = pos=(6,20,2.4) rot=(0,0,1;0rad)
  Radius = 3.35
FEATURE [Part::Sphere] Sphere034
  Angle1 = -90
  Angle2 = 90
  Angle3 = 360
  AttacherType = Attacher::AttachEngine3D
  Placement = pos=(20,34,2.4) rot=(0,0,1;0rad)
  Radius = 3.35
FEATURE [Part::Box] Box076  label="Cube060"
  AttacherType = Attacher::AttachEngine3D
  Height = 15
  Length = 19.5
  Placement = pos=(-9.75,-9.75,-3) rot=(0,0,1;0rad)
  Width = 19.5
FEATURE [Part::Box] Box077  label="Cube061"
  AttacherType = Attacher::AttachEngine3D
  Height = 15
  Length = 11
  Placement = pos=(8,24,-3) rot=(0,0,1;0.785398rad)
  Width = 11
FEATURE [Part::Box] Box078  label="Cube062"
  AttacherType = Attacher::AttachEngine3D
  Height = 15
  Length = 11
  Placement = pos=(8,0,-3) rot=(0,0,1;0.785398rad)
  Width = 11
FEATURE [Part::Box] Box079  label="Cube063"
  AttacherType = Attacher::AttachEngine3D
  Height = 15
  Length = 11
  Placement = pos=(32,0,-3) rot=(0,0,1;0.785398rad)
  Width = 11
FEATURE [Part::Box] Box080  label="Cube064"
  AttacherType = Attacher::AttachEngine3D
  Height = 15
  Length = 11
  Placement = pos=(32,24,-3) rot=(0,0,1;0.785398rad)
  Width = 11
FEATURE [Part::MultiFuse] Fusion022
  Shapes = -> [Box078,Box077,Box079,Box080]
FEATURE [Part::Cylinder] Cylinder020
  Angle = 360
  AttacherType = Attacher::AttachEngine3D
  Height = 20
  Placement = pos=(29.5,10.5,-5) rot=(0,0,1;0rad)
  Radius = 1.9
FEATURE [Part::Cylinder] Cylinder021
  Angle = 360
  AttacherType = Attacher::AttachEngine3D
  Height = 20
  Placement = pos=(10,29.5,-7) rot=(0,0,1;0rad)
  Radius = 1.9
FEATURE [Part::Cylinder] Cylinder022
  Angle = 360
  AttacherType = Attacher::AttachEngine3D
  Height = 20
  Placement = pos=(10,10.5,-5) rot=(0,0,1;0rad)
  Radius = 1.9
FEATURE [Part::Cylinder] Cylinder023
  Angle = 360
  AttacherType = Attacher::AttachEngine3D
  Height = 20
  Placement = pos=(29.5,29.5,-5) rot=(0,0,1;0rad)
  Radius = 1.9
FEATURE [Part::MultiFuse] Fusion023  label="M2 Screw holes001"
  Shapes = -> [Cylinder022,Cylinder020,Cylinder021,Cylinder023]
FEATURE [App::DocumentObjectGroup] Group  label="Cubes"
  Group = -> [Fusion017,Fusion022]
FEATURE [Part::Box] Box083  label="Cube067"
  AttacherType = Attacher::AttachEngine3D
  Height = 10
  Length = 24
  Placement = pos=(-12,-12,2.1) rot=(0,0,1;0rad)
  Width = 24
FEATURE [Part::Box] Box084  label="Cube068"
  AttacherType = Attacher::AttachEngine3D
  Height = 14
  Length = 20
  Placement = pos=(-10,-10,0) rot=(0,0,1;0rad)
  Width = 20
FEATURE [Part::Cut] Cut020
  Base = -> Box083
  Tool = -> Box084
FEATURE [Part::Chamfer] Chamfer007  label="Glue Channel Ball"
  Base = -> Cut020
  Edges = 8 edges r=0.95: [Edge4,Edge5,Edge14,Edge16,Edge17,Edge18,Edge19,Edge20]
FEATURE [Part::Chamfer] Chamfer008  label="Octogon Ball"
  Base = -> Box076
  Edges = 4 edges r=4: [Edge1,Edge3,Edge5,Edge7]
FEATURE [Part::Box] Box085  label="Cube069"
  AttacherType = Attacher::AttachEngine3D
  Height = 15
  Length = 19.5
  Placement = pos=(-9.75,-9.75,-13) rot=(0,0,1;0rad)
  Width = 19.5
FEATURE [Part::Box] Box086  label="Cube070"
  AttacherType = Attacher::AttachEngine3D
  Height = 10
  Length = 10
  Placement = pos=(4,-26,1) rot=(0.205904,-0.974848,-0.085288;0.803573rad)
  Width = 15
FEATURE [Part::Box] Box089  label="Cube073"
  AttacherType = Attacher::AttachEngine3D
  Height = 10
  Length = 10
  Placement = pos=(17,32.0919,9.95) rot=(-0.225436,0.969773,-0.093378;0.807337rad)
  Width = 15
FEATURE [Part::Box] Box090  label="Cube074"
  AttacherType = Attacher::AttachEngine3D
  Height = 10
  Length = 15
  Placement = pos=(30.8481,15.8,2.86019) rot=(0.974848,0.205904,-0.085288;0.803573rad)
  Width = 10
FEATURE [Part::Box] Box091  label="Cube075"
  AttacherType = Attacher::AttachEngine3D
  Height = 10
  Length = 10
  Placement = pos=(7.9081,17,9.95) rot=(-0.450607,0.280623,0.847469;1.65638rad)
  Width = 15
FEATURE [Part::Box] Box092  label="Cube076"
  AttacherType = Attacher::AttachEngine3D
  Height = 10
  Length = 10
  Placement = pos=(23,7.9081,9.95) rot=(-0.381178,-0.08861,0.920245;3.06822rad)
  Width = 15
FEATURE [Part::Box] Box093  label="Cube077"
  AttacherType = Attacher::AttachEngine3D
  Height = 7
  Length = 5
  Width = 40
FEATURE [Part::Box] Box094  label="Cube078"
  AttacherType = Attacher::AttachEngine3D
  Height = 7
  Length = 10
  Placement = pos=(-10,6,0) rot=(0,0,1;0rad)
  Width = 2
FEATURE [Part::Box] Box095  label="Cube079"
  AttacherType = Attacher::AttachEngine3D
  Height = 7
  Length = 10
  Placement = pos=(-10,10,0) rot=(0,0,1;0rad)
  Width = 2
FEATURE [Part::Box] Box096  label="Cube080"
  AttacherType = Attacher::AttachEngine3D
  Height = 7
  Length = 10
  Placement = pos=(-10,25.4,0) rot=(0,0,1;0rad)
  Width = 2
FEATURE [Part::Box] Box097  label="Cube081"
  AttacherType = Attacher::AttachEngine3D
  Height = 7
  Length = 10
  Placement = pos=(-10,34.6,0) rot=(0,0,1;0rad)
  Width = 2
FEATURE [Part::Sphere] Sphere035
  Angle1 = -90
  Angle2 = 90
  Angle3 = 360
  AttacherType = Attacher::AttachEngine3D
  Placement = pos=(-3,6.5,2.5) rot=(0,0,1;0rad)
  Radius = 1.25
FEATURE [Part::Box] Box098  label="Cube082"
  AttacherType = Attacher::AttachEngine3D
  Height = 10
  Length = 13
  Placement = pos=(-10.19,0,-1.19) rot=(0,-1,0;0.785398rad)
  Width = 40
FEATURE [Part::Sphere] Sphere036
  Angle1 = -90
  Angle2 = 90
  Angle3 = 360
  AttacherType = Attacher::AttachEngine3D
  Placement = pos=(-3,11.5,2.5) rot=(0,0,1;0rad)
  Radius = 1.25
FEATURE [Part::Sphere] Sphere037
  Angle1 = -90
  Angle2 = 90
  Angle3 = 360
  AttacherType = Attacher::AttachEngine3D
  Placement = pos=(-3,28,2.5) rot=(0,0,1;0rad)
  Radius = 1.5
FEATURE [Part::Sphere] Sphere038
  Angle1 = -90
  Angle2 = 90
  Angle3 = 360
  AttacherType = Attacher::AttachEngine3D
  Placement = pos=(-3,34,2.5) rot=(0,0,1;0rad)
  Radius = 1.5
FEATURE [Part::MultiFuse] Fusion030
  Shapes = -> [Box093,Box094,Box095,Box096,Box097]
FEATURE [Part::Cut] Cut025
  Base = -> Fusion030
  Tool = -> Box098
FEATURE [Part::MultiFuse] Fusion031
  Shapes = -> [Sphere035,Sphere036,Cut025]
FEATURE [Part::MultiFuse] Fusion032
  Shapes = -> [Sphere038,Sphere037]
FEATURE [Part::Cut] Cut026
  Base = -> Fusion031
  Tool = -> Fusion032
FEATURE [Part::Chamfer] Chamfer009
  Base = -> Cut026
  Edges = 4 edges r=4: [Edge31,Edge37,Edge43,Edge46]
FEATURE [Part::Box] Box099  label="Cube083"
  AttacherType = Attacher::AttachEngine3D
  Height = 7
  Length = 4
  Placement = pos=(-1,5,0) rot=(0,0,1;0rad)
  Width = 1
FEATURE [Part::Box] Box100  label="Cube084"
  AttacherType = Attacher::AttachEngine3D
  Height = 7
  Length = 4
  Placement = pos=(-1,8,0) rot=(0,0,1;0rad)
  Width = 2
FEATURE [Part::Box] Box101  label="Cube085"
  AttacherType = Attacher::AttachEngine3D
  Height = 7
  Length = 4
  Placement = pos=(-1,12,0) rot=(0,0,1;0rad)
  Width = 1
FEATURE [Part::Box] Box102  label="Cube086"
  AttacherType = Attacher::AttachEngine3D
  Height = 7
  Length = 4
  Placement = pos=(-1,24.4,0) rot=(0,0,1;0rad)
  Width = 1
FEATURE [Part::Box] Box103  label="Cube087"
  AttacherType = Attacher::AttachEngine3D
  Height = 7
  Length = 4
  Placement = pos=(-1,36.6,0) rot=(0,0,1;0rad)
  Width = 1
FEATURE [Part::Box] Box104  label="Cube088"
  AttacherType = Attacher::AttachEngine3D
  Height = 7
  Length = 4
  Placement = pos=(-1,27.4,0) rot=(0,0,1;0rad)
  Width = 7.2
FEATURE [Part::MultiFuse] Fusion033
  Shapes = -> [Box104,Box101,Box103,Box100,Box102,Box099]
FEATURE [Part::Cut] Cut027
  Base = -> Chamfer009
  Placement = pos=(-5,40,3) rot=(1,0,0;3.14159rad)
  Tool = -> Fusion033
FEATURE [Part::Box] Box105  label="Cube089"
  AttacherType = Attacher::AttachEngine3D
  Height = 10
  Length = 12
  Placement = pos=(-11,-2,-12) rot=(0,0,1;0rad)
  Width = 44
FEATURE [Part::Cut] Cut028
  Base = -> Cut027
  Tool = -> Box105
FEATURE [Part::Box] Box106  label="Cube090"
  AttacherType = Attacher::AttachEngine3D
  Height = 7
  Length = 10
  Placement = pos=(-10,34.6,0) rot=(0,0,1;0rad)
  Width = 2
FEATURE [Part::Box] Box107  label="Cube091"
  AttacherType = Attacher::AttachEngine3D
  Height = 7
  Length = 5
  Width = 40
FEATURE [Part::Box] Box108  label="Cube092"
  AttacherType = Attacher::AttachEngine3D
  Height = 7
  Length = 10
  Placement = pos=(-10,25.4,0) rot=(0,0,1;0rad)
  Width = 2
FEATURE [Part::Box] Box109  label="Cube093"
  AttacherType = Attacher::AttachEngine3D
  Height = 7
  Length = 10
  Placement = pos=(-10,10,0) rot=(0,0,1;0rad)
  Width = 2
FEATURE [Part::Box] Box110  label="Cube094"
  AttacherType = Attacher::AttachEngine3D
  Height = 7
  Length = 10
  Placement = pos=(-10,6,0) rot=(0,0,1;0rad)
  Width = 2
FEATURE [Part::Sphere] Sphere039
  Angle1 = -90
  Angle2 = 90
  Angle3 = 360
  AttacherType = Attacher::AttachEngine3D
  Placement = pos=(-3,6.5,2.5) rot=(0,0,1;0rad)
  Radius = 1.25
FEATURE [Part::Box] Box111  label="Cube095"
  AttacherType = Attacher::AttachEngine3D
  Height = 10
  Length = 13
  Placement = pos=(-10.19,0,-1.19) rot=(0,-1,0;0.785398rad)
  Width = 40
FEATURE [Part::Sphere] Sphere040
  Angle1 = -90
  Angle2 = 90
  Angle3 = 360
  AttacherType = Attacher::AttachEngine3D
  Placement = pos=(-3,11.5,2.5) rot=(0,0,1;0rad)
  Radius = 1.25
FEATURE [Part::Sphere] Sphere041
  Angle1 = -90
  Angle2 = 90
  Angle3 = 360
  AttacherType = Attacher::AttachEngine3D
  Placement = pos=(-3,28,2.5) rot=(0,0,1;0rad)
  Radius = 1.5
FEATURE [Part::Sphere] Sphere042
  Angle1 = -90
  Angle2 = 90
  Angle3 = 360
  AttacherType = Attacher::AttachEngine3D
  Placement = pos=(-3,34,2.5) rot=(0,0,1;0rad)
  Radius = 1.5
FEATURE [Part::MultiFuse] Fusion034
  Shapes = -> [Box107,Box110,Box109,Box108,Box106]
FEATURE [Part::Cut] Cut029
  Base = -> Fusion034
  Tool = -> Box111
FEATURE [Part::MultiFuse] Fusion035
  Shapes = -> [Sphere039,Sphere040,Cut029]
FEATURE [Part::MultiFuse] Fusion036
  Shapes = -> [Sphere042,Sphere041]
FEATURE [Part::Cut] Cut030
  Base = -> Fusion035
  Tool = -> Fusion036
FEATURE [Part::Chamfer] Chamfer010
  Base = -> Cut030
  Edges = 4 edges r=4: [Edge31,Edge37,Edge43,Edge46]
FEATURE [Part::Box] Box112  label="Cube096"
  AttacherType = Attacher::AttachEngine3D
  Height = 7
  Length = 4
  Placement = pos=(-1,5,0) rot=(0,0,1;0rad)
  Width = 1
FEATURE [Part::Box] Box113  label="Cube097"
  AttacherType = Attacher::AttachEngine3D
  Height = 7
  Length = 4
  Placement = pos=(-1,8,0) rot=(0,0,1;0rad)
  Width = 2
FEATURE [Part::Box] Box114  label="Cube098"
  AttacherType = Attacher::AttachEngine3D
  Height = 7
  Length = 4
  Placement = pos=(-1,12,0) rot=(0,0,1;0rad)
  Width = 1
FEATURE [Part::Box] Box115  label="Cube099"
  AttacherType = Attacher::AttachEngine3D
  Height = 7
  Length = 4
  Placement = pos=(-1,24.4,0) rot=(0,0,1;0rad)
  Width = 1
FEATURE [Part::Box] Box116  label="Cube100"
  AttacherType = Attacher::AttachEngine3D
  Height = 7
  Length = 4
  Placement = pos=(-1,36.6,0) rot=(0,0,1;0rad)
  Width = 1
FEATURE [Part::Box] Box117  label="Cube101"
  AttacherType = Attacher::AttachEngine3D
  Height = 7
  Length = 4
  Placement = pos=(-1,27.4,0) rot=(0,0,1;0rad)
  Width = 7.2
FEATURE [Part::MultiFuse] Fusion037
  Shapes = -> [Box117,Box114,Box116,Box113,Box115,Box112]
FEATURE [Part::Cut] Cut031
  Base = -> Chamfer010
  Placement = pos=(-5,40,3) rot=(1,0,0;3.14159rad)
  Tool = -> Fusion037
FEATURE [Part::Box] Box118  label="Cube102"
  AttacherType = Attacher::AttachEngine3D
  Height = 10
  Length = 12
  Placement = pos=(-11,-2,-12) rot=(0,0,1;0rad)
  Width = 44
FEATURE [Part::Cut] Cut032
  Base = -> Cut031
  Placement = pos=(40,0,0) rot=(0,0,1;1.5708rad)
  Tool = -> Box118
FEATURE [Part::Box] Box119  label="Cube103"
  AttacherType = Attacher::AttachEngine3D
  Height = 7
  Length = 4
  Placement = pos=(-1,12,0) rot=(0,0,1;0rad)
  Width = 1
FEATURE [Part::Box] Box120  label="Cube104"
  AttacherType = Attacher::AttachEngine3D
  Height = 10
  Length = 13
  Placement = pos=(-10.19,0,-1.19) rot=(0,-1,0;0.785398rad)
  Width = 40
FEATURE [Part::Box] Box121  label="Cube105"
  AttacherType = Attacher::AttachEngine3D
  Height = 7
  Length = 4
  Placement = pos=(-1,27.4,0) rot=(0,0,1;0rad)
  Width = 7.2
FEATURE [Part::Box] Box122  label="Cube106"
  AttacherType = Attacher::AttachEngine3D
  Height = 7
  Length = 4
  Placement = pos=(-1,5,0) rot=(0,0,1;0rad)
  Width = 1
FEATURE [Part::Box] Box123  label="Cube107"
  AttacherType = Attacher::AttachEngine3D
  Height = 7
  Length = 10
  Placement = pos=(-10,6,0) rot=(0,0,1;0rad)
  Width = 2
FEATURE [Part::Box] Box124  label="Cube108"
  AttacherType = Attacher::AttachEngine3D
  Height = 10
  Length = 12
  Placement = pos=(-11,-2,-12) rot=(0,0,1;0rad)
  Width = 44
FEATURE [Part::Sphere] Sphere043
  Angle1 = -90
  Angle2 = 90
  Angle3 = 360
  AttacherType = Attacher::AttachEngine3D
  Placement = pos=(-3,6.5,2.5) rot=(0,0,1;0rad)
  Radius = 1.25
FEATURE [Part::Box] Box125  label="Cube109"
  AttacherType = Attacher::AttachEngine3D
  Height = 7
  Length = 10
  Placement = pos=(-10,25.4,0) rot=(0,0,1;0rad)
  Width = 2
FEATURE [Part::Box] Box126  label="Cube110"
  AttacherType = Attacher::AttachEngine3D
  Height = 7
  Length = 10
  Placement = pos=(-10,10,0) rot=(0,0,1;0rad)
  Width = 2
FEATURE [Part::Sphere] Sphere044
  Angle1 = -90
  Angle2 = 90
  Angle3 = 360
  AttacherType = Attacher::AttachEngine3D
  Placement = pos=(-3,28,2.5) rot=(0,0,1;0rad)
  Radius = 1.5
FEATURE [Part::Sphere] Sphere045
  Angle1 = -90
  Angle2 = 90
  Angle3 = 360
  AttacherType = Attacher::AttachEngine3D
  Placement = pos=(-3,11.5,2.5) rot=(0,0,1;0rad)
  Radius = 1.25
FEATURE [Part::Box] Box127  label="Cube111"
  AttacherType = Attacher::AttachEngine3D
  Height = 7
  Length = 4
  Placement = pos=(-1,36.6,0) rot=(0,0,1;0rad)
  Width = 1
FEATURE [Part::Sphere] Sphere046
  Angle1 = -90
  Angle2 = 90
  Angle3 = 360
  AttacherType = Attacher::AttachEngine3D
  Placement = pos=(-3,34,2.5) rot=(0,0,1;0rad)
  Radius = 1.5
FEATURE [Part::MultiFuse] Fusion040
  Shapes = -> [Sphere046,Sphere044]
FEATURE [Part::Box] Box128  label="Cube112"
  AttacherType = Attacher::AttachEngine3D
  Height = 7
  Length = 4
  Placement = pos=(-1,8,0) rot=(0,0,1;0rad)
  Width = 2
FEATURE [Part::Box] Box129  label="Cube113"
  AttacherType = Attacher::AttachEngine3D
  Height = 7
  Length = 10
  Placement = pos=(-10,34.6,0) rot=(0,0,1;0rad)
  Width = 2
FEATURE [Part::Box] Box130  label="Cube114"
  AttacherType = Attacher::AttachEngine3D
  Height = 7
  Length = 4
  Placement = pos=(-1,24.4,0) rot=(0,0,1;0rad)
  Width = 1
FEATURE [Part::MultiFuse] Fusion038
  Shapes = -> [Box121,Box119,Box127,Box128,Box130,Box122]
FEATURE [Part::Box] Box131  label="Cube115"
  AttacherType = Attacher::AttachEngine3D
  Height = 7
  Length = 5
  Width = 40
FEATURE [Part::MultiFuse] Fusion041
  Shapes = -> [Box131,Box123,Box126,Box125,Box129]
FEATURE [Part::Cut] Cut035
  Base = -> Fusion041
  Tool = -> Box120
FEATURE [Part::MultiFuse] Fusion039
  Shapes = -> [Sphere043,Sphere045,Cut035]
FEATURE [Part::Cut] Cut036
  Base = -> Fusion039
  Tool = -> Fusion040
FEATURE [Part::Chamfer] Chamfer011
  Base = -> Cut036
  Edges = 4 edges r=4: [Edge31,Edge37,Edge43,Edge46]
FEATURE [Part::Cut] Cut034
  Base = -> Chamfer011
  Placement = pos=(-5,40,3) rot=(1,0,0;3.14159rad)
  Tool = -> Fusion038
FEATURE [Part::Cut] Cut033
  Base = -> Cut034
  Placement = pos=(40,40,0) rot=(0,0,1;3.14159rad)
  Tool = -> Box124
FEATURE [Part::Sphere] Sphere047
  Angle1 = -90
  Angle2 = 90
  Angle3 = 360
  AttacherType = Attacher::AttachEngine3D
  Placement = pos=(-3,11.5,2.5) rot=(0,0,1;0rad)
  Radius = 1.25
FEATURE [Part::Box] Box132  label="Cube116"
  AttacherType = Attacher::AttachEngine3D
  Height = 7
  Length = 10
  Placement = pos=(-10,6,0) rot=(0,0,1;0rad)
  Width = 2
FEATURE [Part::Box] Box133  label="Cube117"
  AttacherType = Attacher::AttachEngine3D
  Height = 7
  Length = 4
  Placement = pos=(-1,8,0) rot=(0,0,1;0rad)
  Width = 2
FEATURE [Part::Box] Box134  label="Cube118"
  AttacherType = Attacher::AttachEngine3D
  Height = 7
  Length = 10
  Placement = pos=(-10,10,0) rot=(0,0,1;0rad)
  Width = 2
FEATURE [Part::Box] Box135  label="Cube119"
  AttacherType = Attacher::AttachEngine3D
  Height = 10
  Length = 12
  Placement = pos=(-11,-2,-12) rot=(0,0,1;0rad)
  Width = 44
FEATURE [Part::Box] Box136  label="Cube120"
  AttacherType = Attacher::AttachEngine3D
  Height = 7
  Length = 4
  Placement = pos=(-1,5,0) rot=(0,0,1;0rad)
  Width = 1
FEATURE [Part::Sphere] Sphere048
  Angle1 = -90
  Angle2 = 90
  Angle3 = 360
  AttacherType = Attacher::AttachEngine3D
  Placement = pos=(-3,28,2.5) rot=(0,0,1;0rad)
  Radius = 1.5
FEATURE [Part::Sphere] Sphere049
  Angle1 = -90
  Angle2 = 90
  Angle3 = 360
  AttacherType = Attacher::AttachEngine3D
  Placement = pos=(-3,6.5,2.5) rot=(0,0,1;0rad)
  Radius = 1.25
FEATURE [Part::Sphere] Sphere050
  Angle1 = -90
  Angle2 = 90
  Angle3 = 360
  AttacherType = Attacher::AttachEngine3D
  Placement = pos=(-3,34,2.5) rot=(0,0,1;0rad)
  Radius = 1.5
FEATURE [Part::Box] Box137  label="Cube121"
  AttacherType = Attacher::AttachEngine3D
  Height = 7
  Length = 4
  Placement = pos=(-1,12,0) rot=(0,0,1;0rad)
  Width = 1
FEATURE [Part::Box] Box138  label="Cube122"
  AttacherType = Attacher::AttachEngine3D
  Height = 7
  Length = 5
  Width = 40
FEATURE [Part::Box] Box139  label="Cube123"
  AttacherType = Attacher::AttachEngine3D
  Height = 7
  Length = 4
  Placement = pos=(-1,36.6,0) rot=(0,0,1;0rad)
  Width = 1
FEATURE [Part::Box] Box140  label="Cube124"
  AttacherType = Attacher::AttachEngine3D
  Height = 7
  Length = 4
  Placement = pos=(-1,24.4,0) rot=(0,0,1;0rad)
  Width = 1
FEATURE [Part::Box] Box141  label="Cube125"
  AttacherType = Attacher::AttachEngine3D
  Height = 7
  Length = 10
  Placement = pos=(-10,25.4,0) rot=(0,0,1;0rad)
  Width = 2
FEATURE [Part::Box] Box142  label="Cube126"
  AttacherType = Attacher::AttachEngine3D
  Height = 10
  Length = 13
  Placement = pos=(-10.19,0,-1.19) rot=(0,-1,0;0.785398rad)
  Width = 40
FEATURE [Part::Box] Box143  label="Cube127"
  AttacherType = Attacher::AttachEngine3D
  Height = 7
  Length = 10
  Placement = pos=(-10,34.6,0) rot=(0,0,1;0rad)
  Width = 2
FEATURE [Part::MultiFuse] Fusion044
  Shapes = -> [Box138,Box132,Box134,Box141,Box143]
FEATURE [Part::Cut] Cut037
  Base = -> Fusion044
  Tool = -> Box142
FEATURE [Part::MultiFuse] Fusion042
  Shapes = -> [Sphere049,Sphere047,Cut037]
FEATURE [Part::MultiFuse] Fusion045
  Shapes = -> [Sphere050,Sphere048]
FEATURE [Part::Cut] Cut038
  Base = -> Fusion042
  Tool = -> Fusion045
FEATURE [Part::Chamfer] Chamfer012
  Base = -> Cut038
  Edges = 4 edges r=4: [Edge31,Edge37,Edge43,Edge46]
FEATURE [Part::Box] Box144  label="Cube128"
  AttacherType = Attacher::AttachEngine3D
  Height = 7
  Length = 4
  Placement = pos=(-1,27.4,0) rot=(0,0,1;0rad)
  Width = 7.2
FEATURE [Part::MultiFuse] Fusion043
  Shapes = -> [Box144,Box137,Box139,Box133,Box140,Box136]
FEATURE [Part::Cut] Cut040
  Base = -> Chamfer012
  Placement = pos=(-5,40,3) rot=(1,0,0;3.14159rad)
  Tool = -> Fusion043
FEATURE [Part::Cut] Cut039
  Base = -> Cut040
  Placement = pos=(0,40,0) rot=(0,0,-1;1.5708rad)
  Tool = -> Box135
FEATURE [Part::MultiFuse] Fusion048
  Shapes = -> [Box089,Box091,Box090,Box092]
FEATURE [Part::Box] Box145  label="Cube129"
  AttacherType = Attacher::AttachEngine3D
  Height = 15
  Length = 19.5
  Placement = pos=(-9.75,-9.75,-13) rot=(0,0,1;0rad)
  Width = 19.5
FEATURE [Part::Box] Box146  label="Cube130"
  AttacherType = Attacher::AttachEngine3D
  Height = 15
  Length = 19.5
  Placement = pos=(-9.75,-9.75,-3) rot=(0,0,1;0rad)
  Width = 19.5
FEATURE [Part::Chamfer] Chamfer013  label="Octagon"
  Base = -> Box146
  Edges = 4 edges r=4: [Edge1,Edge3,Edge5,Edge7]
FEATURE [Part::Box] Box147  label="Cube131"
  AttacherType = Attacher::AttachEngine3D
  Height = 10
  Length = 24
  Placement = pos=(-12,-12,2.1) rot=(0,0,1;0rad)
  Width = 24
FEATURE [Part::Box] Box148  label="Cube132"
  AttacherType = Attacher::AttachEngine3D
  Height = 14
  Length = 20
  Placement = pos=(-10,-10,0) rot=(0,0,1;0rad)
  Width = 20
FEATURE [Part::Cut] Cut043
  Base = -> Box147
  Tool = -> Box148
FEATURE [Part::Chamfer] Chamfer014  label="Glue Channel"
  Base = -> Cut043
  Edges = 8 edges r=0.95: [Edge4,Edge5,Edge14,Edge16,Edge17,Edge18,Edge19,Edge20]
FEATURE [Part::Cut] Cut047
  Base = -> Cut003
  Tool = -> Chamfer007
FEATURE [Part::Cylinder] Cylinder024
  Angle = 360
  AttacherType = Attacher::AttachEngine3D
  Height = 10
  Placement = pos=(-15,-15,-5) rot=(0,0,1;0rad)
  Radius = 1.7
FEATURE [Part::Cylinder] Cylinder025
  Angle = 360
  AttacherType = Attacher::AttachEngine3D
  Height = 10
  Placement = pos=(15,0,-5) rot=(0,0,1;0rad)
  Radius = 1.7
FEATURE [Part::Cylinder] Cylinder026
  Angle = 360
  AttacherType = Attacher::AttachEngine3D
  Height = 10
  Placement = pos=(-15,15,-5) rot=(0,0,1;0rad)
  Radius = 1.7
FEATURE [Part::MultiFuse] Fusion052  label="Screw Holes to remove ball mags"
  Shapes = -> [Cylinder024,Cylinder025,Cylinder026]
FEATURE [Drawing::FeatureViewAnnotation] Annotation
  Font = Sans
  Rotation = 0
  Scale = 7
  Text = 0.4Added in Holes to Mag plate for removal of magnet
  ViewResult = <g transform="translate(14,23) rotate(0)">\n<text id="Annotation"\n font-family="Sans"\n font-size="7"\n fill="#000000">\n<tspan x="0" dy="1em">0.4Added in Holes to Mag plate for removal of magnet</tspan>\n</text>\n</g>
  Visible = false
  X = 14
  Y = 23
FEATURE [Part::Box] Box149  label="Re-level Edge Clip Block001"
  AttacherType = Attacher::AttachEngine3D
  Height = 10
  Length = 12
  Placement = pos=(-21.5,-2,-7) rot=(0,0,1;0rad)
  Width = 44
FEATURE [Part::Fuse] Fusion  label="Bumps"
  Base = -> Sphere008
  Tool = -> Sphere009
FEATURE [Part::Fuse] Fusion053  label="Holes"
  Base = -> Sphere010
  Tool = -> Sphere011
FEATURE [Part::MultiFuse] Fusion054
  Shapes = -> [Box001,Box002,Box003,Box004,Box005]
FEATURE [Part::Fuse] Fusion055
  Base = -> Fusion
  Tool = -> Fusion054
FEATURE [Part::Cut] Cut
  Base = -> Fusion055
  Tool = -> Fusion053
FEATURE [Part::Cut] Cut056
  Base = -> Cut
  Tool = -> Fusion003
FEATURE [Part::Cut] Cut057
  Base = -> Cut056
  Tool = -> Box013
FEATURE [Part::Cut] Cut058
  Base = -> Cut057
  Tool = -> Box149
FEATURE [Part::Cut] Cut059  label="Edge Clips Master"
  Base = -> Cut058
  Placement = pos=(-20,-20,0) rot=(0,0,1;0rad)
  Tool = -> Box006
FEATURE [Part::Box] Box150  label="Cube133"
  AttacherType = Attacher::AttachEngine3D
  Height = 7
  Length = 5
  Placement = pos=(-5,0,-2) rot=(0,0,1;0rad)
  Width = 40
FEATURE [Part::Box] Box151  label="Cube134"
  AttacherType = Attacher::AttachEngine3D
  Height = 7
  Length = 10
  Placement = pos=(-15,6,-2) rot=(0,0,1;0rad)
  Width = 2
FEATURE [Part::Box] Box152  label="Cube135"
  AttacherType = Attacher::AttachEngine3D
  Height = 7
  Length = 10
  Placement = pos=(-15,10,-2) rot=(0,0,1;0rad)
  Width = 2
FEATURE [Part::Box] Box153  label="Cube136"
  AttacherType = Attacher::AttachEngine3D
  Height = 7
  Length = 10
  Placement = pos=(-15,25.4,-2) rot=(0,0,1;0rad)
  Width = 2
FEATURE [Part::Box] Box154  label="Cube137"
  AttacherType = Attacher::AttachEngine3D
  Height = 7
  Length = 10
  Placement = pos=(-15,34.6,-2) rot=(0,0,1;0rad)
  Width = 2
FEATURE [Part::Sphere] Sphere051
  Angle1 = -90
  Angle2 = 90
  Angle3 = 360
  AttacherType = Attacher::AttachEngine3D
  Placement = pos=(-7.5,6.5,0.5) rot=(0,0,1;0rad)
  Radius = 1.25
FEATURE [Part::Box] Box155  label="Chamfer Cube001"
  AttacherType = Attacher::AttachEngine3D
  Height = 10
  Length = 13
  Placement = pos=(-11.69,0,-1.19) rot=(0,-1,0;0.785398rad)
  Width = 40
FEATURE [Part::Sphere] Sphere052
  Angle1 = -90
  Angle2 = 90
  Angle3 = 360
  AttacherType = Attacher::AttachEngine3D
  Placement = pos=(-7.5,11.5,0.5) rot=(0,0,1;0rad)
  Radius = 1.25
FEATURE [Part::Sphere] Sphere053
  Angle1 = -90
  Angle2 = 90
  Angle3 = 360
  AttacherType = Attacher::AttachEngine3D
  Placement = pos=(-7.5,28,0.5) rot=(0,0,1;0rad)
  Radius = 1.5
FEATURE [Part::Sphere] Sphere054
  Angle1 = -90
  Angle2 = 90
  Angle3 = 360
  AttacherType = Attacher::AttachEngine3D
  Placement = pos=(-7.5,34,0.5) rot=(0,0,1;0rad)
  Radius = 1.5
FEATURE [Part::Box] Box156  label="Cube138"
  AttacherType = Attacher::AttachEngine3D
  Height = 7
  Length = 4
  Placement = pos=(-6,5,-2) rot=(0,0,1;0rad)
  Width = 1
FEATURE [Part::Box] Box157  label="Cube139"
  AttacherType = Attacher::AttachEngine3D
  Height = 7
  Length = 4
  Placement = pos=(-6,8,-2) rot=(0,0,1;0rad)
  Width = 2
FEATURE [Part::Box] Box158  label="Cube140"
  AttacherType = Attacher::AttachEngine3D
  Height = 7
  Length = 4
  Placement = pos=(-6,12,-2) rot=(0,0,1;0rad)
  Width = 1
FEATURE [Part::Box] Box159  label="Cube141"
  AttacherType = Attacher::AttachEngine3D
  Height = 7
  Length = 4
  Placement = pos=(-6,24.4,-2) rot=(0,0,1;0rad)
  Width = 1
FEATURE [Part::Box] Box160  label="Cube142"
  AttacherType = Attacher::AttachEngine3D
  Height = 7
  Length = 4
  Placement = pos=(-6,36.6,-2) rot=(0,0,1;0rad)
  Width = 1
FEATURE [Part::Box] Box161  label="Cube143"
  AttacherType = Attacher::AttachEngine3D
  Height = 7
  Length = 4
  Placement = pos=(-6,27.4,-2) rot=(0,0,1;0rad)
  Width = 7.2
FEATURE [Part::MultiFuse] Fusion056  label="Extra Holes for Clips001"
  Shapes = -> [Box161,Box158,Box160,Box157,Box159,Box156]
FEATURE [Part::Box] Box162  label="Re-level Edge Clip Block002"
  AttacherType = Attacher::AttachEngine3D
  Height = 10
  Length = 20
  Placement = pos=(-19,-2,3) rot=(0,0,1;0rad)
  Width = 44
FEATURE [Part::Box] Box163  label="Re-level Edge Clip Block003"
  AttacherType = Attacher::AttachEngine3D
  Height = 10
  Length = 12
  Placement = pos=(-21.5,-2,-7) rot=(0,0,1;0rad)
  Width = 44
FEATURE [Part::Fuse] Fusion057  label="Bumps001"
  Base = -> Sphere051
  Tool = -> Sphere052
FEATURE [Part::Fuse] Fusion058  label="Holes001"
  Base = -> Sphere053
  Tool = -> Sphere054
FEATURE [Part::MultiFuse] Fusion059
  Shapes = -> [Box150,Box151,Box152,Box153,Box154]
FEATURE [Part::Fuse] Fusion060
  Base = -> Fusion057
  Tool = -> Fusion059
FEATURE [Part::Cut] Cut060
  Base = -> Fusion060
  Tool = -> Fusion058
FEATURE [Part::Cut] Cut061
  Base = -> Cut060
  Tool = -> Fusion056
FEATURE [Part::Cut] Cut062
  Base = -> Cut061
  Tool = -> Box162
FEATURE [Part::Cut] Cut063
  Base = -> Cut062
  Tool = -> Box163
FEATURE [Part::Cut] Cut064  label="Copy Edge Clip"
  Base = -> Cut063
  Placement = pos=(-27,20,-7) rot=(0.707107,0,-0.707107;3.14159rad)
  Tool = -> Box155
FEATURE [App::DocumentObjectGroup] Group001  label="Old"
  Group = -> [Cut008,Cut009,Cut015,Cut018,Fusion021,Fusion023,Group,Cut039,Cut028,Cut032,Cut033,Fusion048]
FEATURE [Part::Box] Box164  label="Cube144"
  AttacherType = Attacher::AttachEngine3D
  Height = 7
  Length = 5
  Placement = pos=(-5,0,-2) rot=(0,0,1;0rad)
  Width = 40
FEATURE [Part::Box] Box165  label="Cube145"
  AttacherType = Attacher::AttachEngine3D
  Height = 7
  Length = 10
  Placement = pos=(-15,6,-2) rot=(0,0,1;0rad)
  Width = 2
FEATURE [Part::Box] Box166  label="Cube146"
  AttacherType = Attacher::AttachEngine3D
  Height = 7
  Length = 10
  Placement = pos=(-15,10,-2) rot=(0,0,1;0rad)
  Width = 2
FEATURE [Part::Box] Box167  label="Cube147"
  AttacherType = Attacher::AttachEngine3D
  Height = 7
  Length = 10
  Placement = pos=(-15,25.4,-2) rot=(0,0,1;0rad)
  Width = 2
FEATURE [Part::Box] Box168  label="Cube148"
  AttacherType = Attacher::AttachEngine3D
  Height = 7
  Length = 10
  Placement = pos=(-15,34.6,-2) rot=(0,0,1;0rad)
  Width = 2
FEATURE [Part::Sphere] Sphere055
  Angle1 = -90
  Angle2 = 90
  Angle3 = 360
  AttacherType = Attacher::AttachEngine3D
  Placement = pos=(-7.5,6.5,0.5) rot=(0,0,1;0rad)
  Radius = 1.25
FEATURE [Part::Box] Box169  label="Chamfer Cube002"
  AttacherType = Attacher::AttachEngine3D
  Height = 10
  Length = 13
  Placement = pos=(-11.69,0,-1.19) rot=(0,-1,0;0.785398rad)
  Width = 40
FEATURE [Part::Sphere] Sphere056
  Angle1 = -90
  Angle2 = 90
  Angle3 = 360
  AttacherType = Attacher::AttachEngine3D
  Placement = pos=(-7.5,11.5,0.5) rot=(0,0,1;0rad)
  Radius = 1.25
FEATURE [Part::Sphere] Sphere057
  Angle1 = -90
  Angle2 = 90
  Angle3 = 360
  AttacherType = Attacher::AttachEngine3D
  Placement = pos=(-7.5,28,0.5) rot=(0,0,1;0rad)
  Radius = 1.5
FEATURE [Part::Sphere] Sphere058
  Angle1 = -90
  Angle2 = 90
  Angle3 = 360
  AttacherType = Attacher::AttachEngine3D
  Placement = pos=(-7.5,34,0.5) rot=(0,0,1;0rad)
  Radius = 1.5
FEATURE [Part::Box] Box170  label="Cube149"
  AttacherType = Attacher::AttachEngine3D
  Height = 7
  Length = 4
  Placement = pos=(-6,5,-2) rot=(0,0,1;0rad)
  Width = 1
FEATURE [Part::Box] Box171  label="Cube150"
  AttacherType = Attacher::AttachEngine3D
  Height = 7
  Length = 4
  Placement = pos=(-6,8,-2) rot=(0,0,1;0rad)
  Width = 2
FEATURE [Part::Box] Box172  label="Cube151"
  AttacherType = Attacher::AttachEngine3D
  Height = 7
  Length = 4
  Placement = pos=(-6,12,-2) rot=(0,0,1;0rad)
  Width = 1
FEATURE [Part::Box] Box173  label="Cube152"
  AttacherType = Attacher::AttachEngine3D
  Height = 7
  Length = 4
  Placement = pos=(-6,24.4,-2) rot=(0,0,1;0rad)
  Width = 1
FEATURE [Part::Box] Box174  label="Cube153"
  AttacherType = Attacher::AttachEngine3D
  Height = 7
  Length = 4
  Placement = pos=(-6,36.6,-2) rot=(0,0,1;0rad)
  Width = 1
FEATURE [Part::Box] Box175  label="Cube154"
  AttacherType = Attacher::AttachEngine3D
  Height = 7
  Length = 4
  Placement = pos=(-6,27.4,-2) rot=(0,0,1;0rad)
  Width = 7.2
FEATURE [Part::MultiFuse] Fusion061  label="Extra Holes for Clips002"
  Shapes = -> [Box175,Box172,Box174,Box171,Box173,Box170]
FEATURE [Part::Box] Box176  label="Re-level Edge Clip Block004"
  AttacherType = Attacher::AttachEngine3D
  Height = 10
  Length = 20
  Placement = pos=(-19,-2,3) rot=(0,0,1;0rad)
  Width = 44
FEATURE [Part::Box] Box177  label="Re-level Edge Clip Block005"
  AttacherType = Attacher::AttachEngine3D
  Height = 10
  Length = 12
  Placement = pos=(-21.5,-2,-7) rot=(0,0,1;0rad)
  Width = 44
FEATURE [Part::Fuse] Fusion062  label="Bumps002"
  Base = -> Sphere055
  Tool = -> Sphere056
FEATURE [Part::Fuse] Fusion063  label="Holes002"
  Base = -> Sphere057
  Tool = -> Sphere058
FEATURE [Part::MultiFuse] Fusion064
  Shapes = -> [Box164,Box165,Box166,Box167,Box168]
FEATURE [Part::Fuse] Fusion065
  Base = -> Fusion062
  Tool = -> Fusion064
FEATURE [Part::Cut] Cut065
  Base = -> Fusion065
  Tool = -> Fusion063
FEATURE [Part::Cut] Cut066
  Base = -> Cut065
  Tool = -> Fusion061
FEATURE [Part::Cut] Cut067
  Base = -> Cut066
  Tool = -> Box176
FEATURE [Part::Cut] Cut068
  Base = -> Cut067
  Tool = -> Box177
FEATURE [Part::Cut] Cut069  label="Edge Clips001"
  Base = -> Cut068
  Placement = pos=(20,-20,0) rot=(0,0,1;1.5708rad)
  Tool = -> Box169
FEATURE [Part::Box] Box178  label="Cube155"
  AttacherType = Attacher::AttachEngine3D
  Height = 7
  Length = 5
  Placement = pos=(-5,0,-2) rot=(0,0,1;0rad)
  Width = 40
FEATURE [Part::Box] Box179  label="Cube156"
  AttacherType = Attacher::AttachEngine3D
  Height = 7
  Length = 10
  Placement = pos=(-15,10,-2) rot=(0,0,1;0rad)
  Width = 2
FEATURE [Part::Box] Box180  label="Re-level Edge Clip Block006"
  AttacherType = Attacher::AttachEngine3D
  Height = 10
  Length = 20
  Placement = pos=(-19,-2,3) rot=(0,0,1;0rad)
  Width = 44
FEATURE [Part::Box] Box181  label="Cube157"
  AttacherType = Attacher::AttachEngine3D
  Height = 7
  Length = 4
  Placement = pos=(-6,27.4,-2) rot=(0,0,1;0rad)
  Width = 7.2
FEATURE [Part::Box] Box182  label="Cube158"
  AttacherType = Attacher::AttachEngine3D
  Height = 7
  Length = 4
  Placement = pos=(-6,12,-2) rot=(0,0,1;0rad)
  Width = 1
FEATURE [Part::Sphere] Sphere059
  Angle1 = -90
  Angle2 = 90
  Angle3 = 360
  AttacherType = Attacher::AttachEngine3D
  Placement = pos=(-7.5,6.5,0.5) rot=(0,0,1;0rad)
  Radius = 1.25
FEATURE [Part::Box] Box183  label="Cube159"
  AttacherType = Attacher::AttachEngine3D
  Height = 7
  Length = 10
  Placement = pos=(-15,25.4,-2) rot=(0,0,1;0rad)
  Width = 2
FEATURE [Part::Box] Box184  label="Cube160"
  AttacherType = Attacher::AttachEngine3D
  Height = 7
  Length = 4
  Placement = pos=(-6,36.6,-2) rot=(0,0,1;0rad)
  Width = 1
FEATURE [Part::Sphere] Sphere060
  Angle1 = -90
  Angle2 = 90
  Angle3 = 360
  AttacherType = Attacher::AttachEngine3D
  Placement = pos=(-7.5,34,0.5) rot=(0,0,1;0rad)
  Radius = 1.5
FEATURE [Part::Box] Box185  label="Cube161"
  AttacherType = Attacher::AttachEngine3D
  Height = 7
  Length = 4
  Placement = pos=(-6,24.4,-2) rot=(0,0,1;0rad)
  Width = 1
FEATURE [Part::Box] Box186  label="Cube162"
  AttacherType = Attacher::AttachEngine3D
  Height = 7
  Length = 4
  Placement = pos=(-6,8,-2) rot=(0,0,1;0rad)
  Width = 2
FEATURE [Part::Box] Box187  label="Re-level Edge Clip Block007"
  AttacherType = Attacher::AttachEngine3D
  Height = 10
  Length = 12
  Placement = pos=(-21.5,-2,-7) rot=(0,0,1;0rad)
  Width = 44
FEATURE [Part::Sphere] Sphere061
  Angle1 = -90
  Angle2 = 90
  Angle3 = 360
  AttacherType = Attacher::AttachEngine3D
  Placement = pos=(-7.5,11.5,0.5) rot=(0,0,1;0rad)
  Radius = 1.25
FEATURE [Part::Sphere] Sphere062
  Angle1 = -90
  Angle2 = 90
  Angle3 = 360
  AttacherType = Attacher::AttachEngine3D
  Placement = pos=(-7.5,28,0.5) rot=(0,0,1;0rad)
  Radius = 1.5
FEATURE [Part::Fuse] Fusion066  label="Holes003"
  Base = -> Sphere062
  Tool = -> Sphere060
FEATURE [Part::Box] Box188  label="Cube163"
  AttacherType = Attacher::AttachEngine3D
  Height = 7
  Length = 10
  Placement = pos=(-15,34.6,-2) rot=(0,0,1;0rad)
  Width = 2
FEATURE [Part::Box] Box189  label="Cube164"
  AttacherType = Attacher::AttachEngine3D
  Height = 7
  Length = 4
  Placement = pos=(-6,5,-2) rot=(0,0,1;0rad)
  Width = 1
FEATURE [Part::MultiFuse] Fusion067  label="Extra Holes for Clips003"
  Shapes = -> [Box181,Box182,Box184,Box186,Box185,Box189]
FEATURE [Part::Box] Box190  label="Cube165"
  AttacherType = Attacher::AttachEngine3D
  Height = 7
  Length = 10
  Placement = pos=(-15,6,-2) rot=(0,0,1;0rad)
  Width = 2
FEATURE [Part::MultiFuse] Fusion069
  Shapes = -> [Box178,Box190,Box179,Box183,Box188]
FEATURE [Part::Fuse] Fusion070  label="Bumps003"
  Base = -> Sphere059
  Tool = -> Sphere061
FEATURE [Part::Fuse] Fusion068
  Base = -> Fusion070
  Tool = -> Fusion069
FEATURE [Part::Cut] Cut073
  Base = -> Fusion068
  Tool = -> Fusion066
FEATURE [Part::Cut] Cut070
  Base = -> Cut073
  Tool = -> Fusion067
FEATURE [Part::Cut] Cut071
  Base = -> Cut070
  Tool = -> Box180
FEATURE [Part::Cut] Cut072
  Base = -> Cut071
  Tool = -> Box187
FEATURE [Part::Box] Box191  label="Chamfer Cube003"
  AttacherType = Attacher::AttachEngine3D
  Height = 10
  Length = 13
  Placement = pos=(-11.69,0,-1.19) rot=(0,-1,0;0.785398rad)
  Width = 40
FEATURE [Part::Cut] Cut074  label="Edge Clips002"
  Base = -> Cut072
  Placement = pos=(20,20,0) rot=(0,0,1;3.14159rad)
  Tool = -> Box191
FEATURE [Part::Box] Box192  label="Cube166"
  AttacherType = Attacher::AttachEngine3D
  Height = 7
  Length = 10
  Placement = pos=(-15,6,-2) rot=(0,0,1;0rad)
  Width = 2
FEATURE [Part::Box] Box193  label="Chamfer Cube004"
  AttacherType = Attacher::AttachEngine3D
  Height = 10
  Length = 13
  Placement = pos=(-11.69,0,-1.19) rot=(0,-1,0;0.785398rad)
  Width = 40
FEATURE [Part::Box] Box194  label="Re-level Edge Clip Block008"
  AttacherType = Attacher::AttachEngine3D
  Height = 10
  Length = 20
  Placement = pos=(-19,-2,3) rot=(0,0,1;0rad)
  Width = 44
FEATURE [Part::Box] Box195  label="Cube167"
  AttacherType = Attacher::AttachEngine3D
  Height = 7
  Length = 10
  Placement = pos=(-15,10,-2) rot=(0,0,1;0rad)
  Width = 2
FEATURE [Part::Box] Box196  label="Cube168"
  AttacherType = Attacher::AttachEngine3D
  Height = 7
  Length = 5
  Placement = pos=(-5,0,-2) rot=(0,0,1;0rad)
  Width = 40
FEATURE [Part::Box] Box197  label="Cube169"
  AttacherType = Attacher::AttachEngine3D
  Height = 7
  Length = 4
  Placement = pos=(-6,5,-2) rot=(0,0,1;0rad)
  Width = 1
FEATURE [Part::Box] Box198  label="Cube170"
  AttacherType = Attacher::AttachEngine3D
  Height = 7
  Length = 4
  Placement = pos=(-6,12,-2) rot=(0,0,1;0rad)
  Width = 1
FEATURE [Part::Box] Box199  label="Cube171"
  AttacherType = Attacher::AttachEngine3D
  Height = 7
  Length = 4
  Placement = pos=(-6,27.4,-2) rot=(0,0,1;0rad)
  Width = 7.2
FEATURE [Part::Box] Box200  label="Cube172"
  AttacherType = Attacher::AttachEngine3D
  Height = 7
  Length = 4
  Placement = pos=(-6,24.4,-2) rot=(0,0,1;0rad)
  Width = 1
FEATURE [Part::Sphere] Sphere063
  Angle1 = -90
  Angle2 = 90
  Angle3 = 360
  AttacherType = Attacher::AttachEngine3D
  Placement = pos=(-7.5,28,0.5) rot=(0,0,1;0rad)
  Radius = 1.5
FEATURE [Part::Sphere] Sphere064
  Angle1 = -90
  Angle2 = 90
  Angle3 = 360
  AttacherType = Attacher::AttachEngine3D
  Placement = pos=(-7.5,11.5,0.5) rot=(0,0,1;0rad)
  Radius = 1.25
FEATURE [Part::Box] Box201  label="Cube173"
  AttacherType = Attacher::AttachEngine3D
  Height = 7
  Length = 4
  Placement = pos=(-6,8,-2) rot=(0,0,1;0rad)
  Width = 2
FEATURE [Part::Box] Box202  label="Cube174"
  AttacherType = Attacher::AttachEngine3D
  Height = 7
  Length = 10
  Placement = pos=(-15,25.4,-2) rot=(0,0,1;0rad)
  Width = 2
FEATURE [Part::Sphere] Sphere065
  Angle1 = -90
  Angle2 = 90
  Angle3 = 360
  AttacherType = Attacher::AttachEngine3D
  Placement = pos=(-7.5,6.5,0.5) rot=(0,0,1;0rad)
  Radius = 1.25
FEATURE [Part::Fuse] Fusion073  label="Bumps004"
  Base = -> Sphere065
  Tool = -> Sphere064
FEATURE [Part::Sphere] Sphere066
  Angle1 = -90
  Angle2 = 90
  Angle3 = 360
  AttacherType = Attacher::AttachEngine3D
  Placement = pos=(-7.5,34,0.5) rot=(0,0,1;0rad)
  Radius = 1.5
FEATURE [Part::Fuse] Fusion071  label="Holes004"
  Base = -> Sphere063
  Tool = -> Sphere066
FEATURE [Part::Box] Box203  label="Re-level Edge Clip Block009"
  AttacherType = Attacher::AttachEngine3D
  Height = 10
  Length = 12
  Placement = pos=(-21.5,-2,-7) rot=(0,0,1;0rad)
  Width = 44
FEATURE [Part::Box] Box204  label="Cube175"
  AttacherType = Attacher::AttachEngine3D
  Height = 7
  Length = 4
  Placement = pos=(-6,36.6,-2) rot=(0,0,1;0rad)
  Width = 1
FEATURE [Part::MultiFuse] Fusion074  label="Extra Holes for Clips004"
  Shapes = -> [Box199,Box198,Box204,Box201,Box200,Box197]
FEATURE [Part::Box] Box205  label="Cube176"
  AttacherType = Attacher::AttachEngine3D
  Height = 7
  Length = 10
  Placement = pos=(-15,34.6,-2) rot=(0,0,1;0rad)
  Width = 2
FEATURE [Part::MultiFuse] Fusion072
  Shapes = -> [Box196,Box192,Box195,Box202,Box205]
FEATURE [Part::Fuse] Fusion075
  Base = -> Fusion073
  Tool = -> Fusion072
FEATURE [Part::Cut] Cut075
  Base = -> Fusion075
  Tool = -> Fusion071
FEATURE [Part::Cut] Cut076
  Base = -> Cut075
  Tool = -> Fusion074
FEATURE [Part::Cut] Cut078
  Base = -> Cut076
  Tool = -> Box194
FEATURE [Part::Cut] Cut077
  Base = -> Cut078
  Tool = -> Box203
FEATURE [Part::Cut] Cut079  label="Edge Clips003"
  Base = -> Cut077
  Placement = pos=(-20,20,0) rot=(0,0,-1;1.5708rad)
  Tool = -> Box193
FEATURE [Part::MultiFuse] Fusion076  label="Edge Clips Fusion"
  Shapes = -> [Cut059,Cut069,Cut074,Cut079]
FEATURE [Part::Box] Box206  label="Cube177"
  AttacherType = Attacher::AttachEngine3D
  Height = 10
  Length = 10
  Placement = pos=(26,4,1) rot=(0.442189,-0.287968,0.849437;1.66134rad)
  Width = 15
FEATURE [Part::Box] Box207  label="Cube178"
  AttacherType = Attacher::AttachEngine3D
  Height = 10
  Length = 10
  Placement = pos=(-4,26,1) rot=(0.381439,0.080566,0.920876;3.07487rad)
  Width = 15
FEATURE [Part::Box] Box208  label="Cube179"
  AttacherType = Attacher::AttachEngine3D
  Height = 10
  Length = 10
  Placement = pos=(-26,-4,1) rot=(-0.273007,-0.419215,-0.865867;1.78566rad)
  Width = 15
FEATURE [Part::MultiFuse] Fusion078  label="Glue Dents"
  Shapes = -> [Box086,Box208,Box207,Box206]
FEATURE [Part::Box] Box209  label="Cube180"
  AttacherType = Attacher::AttachEngine3D
  Height = 7
  Length = 5
  Placement = pos=(-5,0,-2) rot=(0,0,1;0rad)
  Width = 40
FEATURE [Part::Box] Box210  label="Cube181"
  AttacherType = Attacher::AttachEngine3D
  Height = 7
  Length = 10
  Placement = pos=(-15,6,-2) rot=(0,0,1;0rad)
  Width = 2
FEATURE [Part::Box] Box211  label="Cube182"
  AttacherType = Attacher::AttachEngine3D
  Height = 7
  Length = 10
  Placement = pos=(-15,10,-2) rot=(0,0,1;0rad)
  Width = 2
FEATURE [Part::Box] Box212  label="Cube183"
  AttacherType = Attacher::AttachEngine3D
  Height = 7
  Length = 10
  Placement = pos=(-15,25.4,-2) rot=(0,0,1;0rad)
  Width = 2
FEATURE [Part::Box] Box213  label="Cube184"
  AttacherType = Attacher::AttachEngine3D
  Height = 7
  Length = 10
  Placement = pos=(-15,34.6,-2) rot=(0,0,1;0rad)
  Width = 2
FEATURE [Part::Sphere] Sphere067
  Angle1 = -90
  Angle2 = 90
  Angle3 = 360
  AttacherType = Attacher::AttachEngine3D
  Placement = pos=(-7.5,6.5,0.5) rot=(0,0,1;0rad)
  Radius = 1.25
FEATURE [Part::Box] Box214  label="Chamfer Cube005"
  AttacherType = Attacher::AttachEngine3D
  Height = 10
  Length = 13
  Placement = pos=(-11.69,0,-1.19) rot=(0,-1,0;0.785398rad)
  Width = 40
FEATURE [Part::Sphere] Sphere068
  Angle1 = -90
  Angle2 = 90
  Angle3 = 360
  AttacherType = Attacher::AttachEngine3D
  Placement = pos=(-7.5,11.5,0.5) rot=(0,0,1;0rad)
  Radius = 1.25
FEATURE [Part::Sphere] Sphere069
  Angle1 = -90
  Angle2 = 90
  Angle3 = 360
  AttacherType = Attacher::AttachEngine3D
  Placement = pos=(-7.5,28,0.5) rot=(0,0,1;0rad)
  Radius = 1.5
FEATURE [Part::Sphere] Sphere070
  Angle1 = -90
  Angle2 = 90
  Angle3 = 360
  AttacherType = Attacher::AttachEngine3D
  Placement = pos=(-7.5,34,0.5) rot=(0,0,1;0rad)
  Radius = 1.5
FEATURE [Part::Box] Box215  label="Cube185"
  AttacherType = Attacher::AttachEngine3D
  Height = 7
  Length = 4
  Placement = pos=(-6,5,-2) rot=(0,0,1;0rad)
  Width = 1
FEATURE [Part::Box] Box216  label="Cube186"
  AttacherType = Attacher::AttachEngine3D
  Height = 7
  Length = 4
  Placement = pos=(-6,8,-2) rot=(0,0,1;0rad)
  Width = 2
FEATURE [Part::Box] Box217  label="Cube187"
  AttacherType = Attacher::AttachEngine3D
  Height = 7
  Length = 4
  Placement = pos=(-6,12,-2) rot=(0,0,1;0rad)
  Width = 1
FEATURE [Part::Box] Box218  label="Cube188"
  AttacherType = Attacher::AttachEngine3D
  Height = 7
  Length = 4
  Placement = pos=(-6,24.4,-2) rot=(0,0,1;0rad)
  Width = 1
FEATURE [Part::Box] Box219  label="Cube189"
  AttacherType = Attacher::AttachEngine3D
  Height = 7
  Length = 4
  Placement = pos=(-6,36.6,-2) rot=(0,0,1;0rad)
  Width = 1
FEATURE [Part::Box] Box220  label="Cube190"
  AttacherType = Attacher::AttachEngine3D
  Height = 7
  Length = 4
  Placement = pos=(-6,27.4,-2) rot=(0,0,1;0rad)
  Width = 7.2
FEATURE [Part::MultiFuse] Fusion079  label="Extra Holes for Clips005"
  Shapes = -> [Box220,Box217,Box219,Box216,Box218,Box215]
FEATURE [Part::Box] Box221  label="Re-level Edge Clip Block010"
  AttacherType = Attacher::AttachEngine3D
  Height = 10
  Length = 20
  Placement = pos=(-19,-2,3) rot=(0,0,1;0rad)
  Width = 44
FEATURE [Part::Box] Box222  label="Re-level Edge Clip Block011"
  AttacherType = Attacher::AttachEngine3D
  Height = 10
  Length = 12
  Placement = pos=(-21.5,-2,-7) rot=(0,0,1;0rad)
  Width = 44
FEATURE [Part::Fuse] Fusion080  label="Bumps005"
  Base = -> Sphere067
  Tool = -> Sphere068
FEATURE [Part::Fuse] Fusion081  label="Holes005"
  Base = -> Sphere069
  Tool = -> Sphere070
FEATURE [Part::MultiFuse] Fusion082
  Shapes = -> [Box209,Box210,Box211,Box212,Box213]
FEATURE [Part::Fuse] Fusion083
  Base = -> Fusion080
  Tool = -> Fusion082
FEATURE [Part::Cut] Cut082
  Base = -> Fusion083
  Tool = -> Fusion081
FEATURE [Part::Cut] Cut083
  Base = -> Cut082
  Tool = -> Fusion079
FEATURE [Part::Cut] Cut084
  Base = -> Cut083
  Tool = -> Box221
FEATURE [Part::Cut] Cut085
  Base = -> Cut084
  Tool = -> Box222
FEATURE [Part::Cut] Cut086  label="Edge Clips Master001"
  Base = -> Cut085
  Placement = pos=(-20,-20,0) rot=(0,0,1;0rad)
  Tool = -> Box214
FEATURE [Part::Box] Box223  label="Cube191"
  AttacherType = Attacher::AttachEngine3D
  Height = 7
  Length = 5
  Placement = pos=(-5,0,-2) rot=(0,0,1;0rad)
  Width = 40
FEATURE [Part::Box] Box224  label="Cube192"
  AttacherType = Attacher::AttachEngine3D
  Height = 7
  Length = 4
  Placement = pos=(-6,8,-2) rot=(0,0,1;0rad)
  Width = 2
FEATURE [Part::Box] Box225  label="Chamfer Cube006"
  AttacherType = Attacher::AttachEngine3D
  Height = 10
  Length = 13
  Placement = pos=(-11.69,0,-1.19) rot=(0,-1,0;0.785398rad)
  Width = 40
FEATURE [Part::Box] Box226  label="Cube193"
  AttacherType = Attacher::AttachEngine3D
  Height = 7
  Length = 10
  Placement = pos=(-15,6,-2) rot=(0,0,1;0rad)
  Width = 2
FEATURE [Part::Sphere] Sphere071
  Angle1 = -90
  Angle2 = 90
  Angle3 = 360
  AttacherType = Attacher::AttachEngine3D
  Placement = pos=(-7.5,11.5,0.5) rot=(0,0,1;0rad)
  Radius = 1.25
FEATURE [Part::Box] Box227  label="Cube194"
  AttacherType = Attacher::AttachEngine3D
  Height = 7
  Length = 4
  Placement = pos=(-6,27.4,-2) rot=(0,0,1;0rad)
  Width = 7.2
FEATURE [Part::Box] Box228  label="Cube195"
  AttacherType = Attacher::AttachEngine3D
  Height = 7
  Length = 4
  Placement = pos=(-6,12,-2) rot=(0,0,1;0rad)
  Width = 1
FEATURE [Part::Box] Box229  label="Cube196"
  AttacherType = Attacher::AttachEngine3D
  Height = 7
  Length = 4
  Placement = pos=(-6,24.4,-2) rot=(0,0,1;0rad)
  Width = 1
FEATURE [Part::Sphere] Sphere072
  Angle1 = -90
  Angle2 = 90
  Angle3 = 360
  AttacherType = Attacher::AttachEngine3D
  Placement = pos=(-7.5,6.5,0.5) rot=(0,0,1;0rad)
  Radius = 1.25
FEATURE [Part::Box] Box230  label="Cube197"
  AttacherType = Attacher::AttachEngine3D
  Height = 7
  Length = 4
  Placement = pos=(-6,36.6,-2) rot=(0,0,1;0rad)
  Width = 1
FEATURE [Part::Box] Box231  label="Cube198"
  AttacherType = Attacher::AttachEngine3D
  Height = 7
  Length = 10
  Placement = pos=(-15,10,-2) rot=(0,0,1;0rad)
  Width = 2
FEATURE [Part::Sphere] Sphere073
  Angle1 = -90
  Angle2 = 90
  Angle3 = 360
  AttacherType = Attacher::AttachEngine3D
  Placement = pos=(-7.5,34,0.5) rot=(0,0,1;0rad)
  Radius = 1.5
FEATURE [Part::Box] Box232  label="Cube199"
  AttacherType = Attacher::AttachEngine3D
  Height = 7
  Length = 4
  Placement = pos=(-6,5,-2) rot=(0,0,1;0rad)
  Width = 1
FEATURE [Part::MultiFuse] Fusion085  label="Extra Holes for Clips006"
  Shapes = -> [Box227,Box228,Box230,Box224,Box229,Box232]
FEATURE [Part::Box] Box233  label="Re-level Edge Clip Block012"
  AttacherType = Attacher::AttachEngine3D
  Height = 10
  Length = 20
  Placement = pos=(-19,-2,3) rot=(0,0,1;0rad)
  Width = 44
FEATURE [Part::Box] Box234  label="Cube200"
  AttacherType = Attacher::AttachEngine3D
  Height = 7
  Length = 10
  Placement = pos=(-15,34.6,-2) rot=(0,0,1;0rad)
  Width = 2
FEATURE [Part::Box] Box235  label="Cube201"
  AttacherType = Attacher::AttachEngine3D
  Height = 7
  Length = 10
  Placement = pos=(-15,25.4,-2) rot=(0,0,1;0rad)
  Width = 2
FEATURE [Part::MultiFuse] Fusion086
  Shapes = -> [Box223,Box226,Box231,Box235,Box234]
FEATURE [Part::Fuse] Fusion087  label="Bumps006"
  Base = -> Sphere072
  Tool = -> Sphere071
FEATURE [Part::Fuse] Fusion084
  Base = -> Fusion087
  Tool = -> Fusion086
FEATURE [Part::Sphere] Sphere074
  Angle1 = -90
  Angle2 = 90
  Angle3 = 360
  AttacherType = Attacher::AttachEngine3D
  Placement = pos=(-7.5,28,0.5) rot=(0,0,1;0rad)
  Radius = 1.5
FEATURE [Part::Fuse] Fusion088  label="Holes006"
  Base = -> Sphere074
  Tool = -> Sphere073
FEATURE [Part::Box] Box236  label="Re-level Edge Clip Block013"
  AttacherType = Attacher::AttachEngine3D
  Height = 10
  Length = 12
  Placement = pos=(-21.5,-2,-7) rot=(0,0,1;0rad)
  Width = 44
FEATURE [Part::Cut] Cut087
  Base = -> Fusion084
  Tool = -> Fusion088
FEATURE [Part::Cut] Cut088
  Base = -> Cut087
  Tool = -> Fusion085
FEATURE [Part::Cut] Cut089
  Base = -> Cut088
  Tool = -> Box233
FEATURE [Part::Cut] Cut090
  Base = -> Cut089
  Tool = -> Box236
FEATURE [Part::Cut] Cut091  label="Edge Clips004"
  Base = -> Cut090
  Placement = pos=(20,-20,0) rot=(0,0,1;1.5708rad)
  Tool = -> Box225
FEATURE [Part::Box] Box237  label="Re-level Edge Clip Block014"
  AttacherType = Attacher::AttachEngine3D
  Height = 10
  Length = 12
  Placement = pos=(-21.5,-2,-7) rot=(0,0,1;0rad)
  Width = 44
FEATURE [Part::Box] Box238  label="Cube202"
  AttacherType = Attacher::AttachEngine3D
  Height = 7
  Length = 4
  Placement = pos=(-6,36.6,-2) rot=(0,0,1;0rad)
  Width = 1
FEATURE [Part::Box] Box239  label="Cube203"
  AttacherType = Attacher::AttachEngine3D
  Height = 7
  Length = 10
  Placement = pos=(-15,10,-2) rot=(0,0,1;0rad)
  Width = 2
FEATURE [Part::Box] Box240  label="Cube204"
  AttacherType = Attacher::AttachEngine3D
  Height = 7
  Length = 10
  Placement = pos=(-15,25.4,-2) rot=(0,0,1;0rad)
  Width = 2
FEATURE [Part::Box] Box241  label="Re-level Edge Clip Block015"
  AttacherType = Attacher::AttachEngine3D
  Height = 10
  Length = 20
  Placement = pos=(-19,-2,3) rot=(0,0,1;0rad)
  Width = 44
FEATURE [Part::Box] Box242  label="Cube205"
  AttacherType = Attacher::AttachEngine3D
  Height = 7
  Length = 10
  Placement = pos=(-15,34.6,-2) rot=(0,0,1;0rad)
  Width = 2
FEATURE [Part::Sphere] Sphere075
  Angle1 = -90
  Angle2 = 90
  Angle3 = 360
  AttacherType = Attacher::AttachEngine3D
  Placement = pos=(-7.5,34,0.5) rot=(0,0,1;0rad)
  Radius = 1.5
FEATURE [Part::Sphere] Sphere076
  Angle1 = -90
  Angle2 = 90
  Angle3 = 360
  AttacherType = Attacher::AttachEngine3D
  Placement = pos=(-7.5,28,0.5) rot=(0,0,1;0rad)
  Radius = 1.5
FEATURE [Part::Fuse] Fusion089  label="Holes007"
  Base = -> Sphere076
  Tool = -> Sphere075
FEATURE [Part::Box] Box243  label="Cube206"
  AttacherType = Attacher::AttachEngine3D
  Height = 7
  Length = 4
  Placement = pos=(-6,5,-2) rot=(0,0,1;0rad)
  Width = 1
FEATURE [Part::Box] Box244  label="Cube207"
  AttacherType = Attacher::AttachEngine3D
  Height = 7
  Length = 4
  Placement = pos=(-6,24.4,-2) rot=(0,0,1;0rad)
  Width = 1
FEATURE [Part::Sphere] Sphere077
  Angle1 = -90
  Angle2 = 90
  Angle3 = 360
  AttacherType = Attacher::AttachEngine3D
  Placement = pos=(-7.5,11.5,0.5) rot=(0,0,1;0rad)
  Radius = 1.25
FEATURE [Part::Box] Box245  label="Cube208"
  AttacherType = Attacher::AttachEngine3D
  Height = 7
  Length = 4
  Placement = pos=(-6,12,-2) rot=(0,0,1;0rad)
  Width = 1
FEATURE [Part::Box] Box246  label="Chamfer Cube007"
  AttacherType = Attacher::AttachEngine3D
  Height = 10
  Length = 13
  Placement = pos=(-11.69,0,-1.19) rot=(0,-1,0;0.785398rad)
  Width = 40
FEATURE [Part::Sphere] Sphere078
  Angle1 = -90
  Angle2 = 90
  Angle3 = 360
  AttacherType = Attacher::AttachEngine3D
  Placement = pos=(-7.5,6.5,0.5) rot=(0,0,1;0rad)
  Radius = 1.25
FEATURE [Part::Fuse] Fusion090  label="Bumps007"
  Base = -> Sphere078
  Tool = -> Sphere077
FEATURE [Part::Box] Box247  label="Cube209"
  AttacherType = Attacher::AttachEngine3D
  Height = 7
  Length = 5
  Placement = pos=(-5,0,-2) rot=(0,0,1;0rad)
  Width = 40
FEATURE [Part::Box] Box248  label="Cube210"
  AttacherType = Attacher::AttachEngine3D
  Height = 7
  Length = 4
  Placement = pos=(-6,27.4,-2) rot=(0,0,1;0rad)
  Width = 7.2
FEATURE [Part::Box] Box249  label="Cube211"
  AttacherType = Attacher::AttachEngine3D
  Height = 7
  Length = 4
  Placement = pos=(-6,8,-2) rot=(0,0,1;0rad)
  Width = 2
FEATURE [Part::MultiFuse] Fusion091  label="Extra Holes for Clips007"
  Shapes = -> [Box248,Box245,Box238,Box249,Box244,Box243]
FEATURE [Part::Box] Box250  label="Cube212"
  AttacherType = Attacher::AttachEngine3D
  Height = 7
  Length = 10
  Placement = pos=(-15,6,-2) rot=(0,0,1;0rad)
  Width = 2
FEATURE [Part::MultiFuse] Fusion092
  Shapes = -> [Box247,Box250,Box239,Box240,Box242]
FEATURE [Part::Fuse] Fusion093
  Base = -> Fusion090
  Tool = -> Fusion092
FEATURE [Part::Cut] Cut093
  Base = -> Fusion093
  Tool = -> Fusion089
FEATURE [Part::Cut] Cut094
  Base = -> Cut093
  Tool = -> Fusion091
FEATURE [Part::Cut] Cut095
  Base = -> Cut094
  Tool = -> Box241
FEATURE [Part::Cut] Cut096
  Base = -> Cut095
  Tool = -> Box237
FEATURE [Part::Cut] Cut092  label="Edge Clips005"
  Base = -> Cut096
  Placement = pos=(20,20,0) rot=(0,0,1;3.14159rad)
  Tool = -> Box246
FEATURE [Part::Box] Box251  label="Re-level Edge Clip Block016"
  AttacherType = Attacher::AttachEngine3D
  Height = 10
  Length = 12
  Placement = pos=(-21.5,-2,-7) rot=(0,0,1;0rad)
  Width = 44
FEATURE [Part::Box] Box252  label="Cube213"
  AttacherType = Attacher::AttachEngine3D
  Height = 7
  Length = 10
  Placement = pos=(-15,10,-2) rot=(0,0,1;0rad)
  Width = 2
FEATURE [Part::Box] Box253  label="Cube214"
  AttacherType = Attacher::AttachEngine3D
  Height = 7
  Length = 4
  Placement = pos=(-6,12,-2) rot=(0,0,1;0rad)
  Width = 1
FEATURE [Part::Box] Box254  label="Chamfer Cube008"
  AttacherType = Attacher::AttachEngine3D
  Height = 10
  Length = 13
  Placement = pos=(-11.69,0,-1.19) rot=(0,-1,0;0.785398rad)
  Width = 40
FEATURE [Part::Sphere] Sphere079
  Angle1 = -90
  Angle2 = 90
  Angle3 = 360
  AttacherType = Attacher::AttachEngine3D
  Placement = pos=(-7.5,6.5,0.5) rot=(0,0,1;0rad)
  Radius = 1.25
FEATURE [Part::Box] Box255  label="Cube215"
  AttacherType = Attacher::AttachEngine3D
  Height = 7
  Length = 5
  Placement = pos=(-5,0,-2) rot=(0,0,1;0rad)
  Width = 40
FEATURE [Part::Box] Box256  label="Cube216"
  AttacherType = Attacher::AttachEngine3D
  Height = 7
  Length = 4
  Placement = pos=(-6,27.4,-2) rot=(0,0,1;0rad)
  Width = 7.2
FEATURE [Part::Box] Box257  label="Cube217"
  AttacherType = Attacher::AttachEngine3D
  Height = 7
  Length = 4
  Placement = pos=(-6,8,-2) rot=(0,0,1;0rad)
  Width = 2
FEATURE [Part::Box] Box258  label="Cube218"
  AttacherType = Attacher::AttachEngine3D
  Height = 7
  Length = 10
  Placement = pos=(-15,6,-2) rot=(0,0,1;0rad)
  Width = 2
FEATURE [Part::Sphere] Sphere080
  Angle1 = -90
  Angle2 = 90
  Angle3 = 360
  AttacherType = Attacher::AttachEngine3D
  Placement = pos=(-7.5,28,0.5) rot=(0,0,1;0rad)
  Radius = 1.5
FEATURE [Part::Box] Box259  label="Cube219"
  AttacherType = Attacher::AttachEngine3D
  Height = 7
  Length = 4
  Placement = pos=(-6,5,-2) rot=(0,0,1;0rad)
  Width = 1
FEATURE [Part::Box] Box260  label="Cube220"
  AttacherType = Attacher::AttachEngine3D
  Height = 7
  Length = 4
  Placement = pos=(-6,24.4,-2) rot=(0,0,1;0rad)
  Width = 1
FEATURE [Part::Sphere] Sphere081
  Angle1 = -90
  Angle2 = 90
  Angle3 = 360
  AttacherType = Attacher::AttachEngine3D
  Placement = pos=(-7.5,11.5,0.5) rot=(0,0,1;0rad)
  Radius = 1.25
FEATURE [Part::Box] Box261  label="Re-level Edge Clip Block017"
  AttacherType = Attacher::AttachEngine3D
  Height = 10
  Length = 20
  Placement = pos=(-19,-2,3) rot=(0,0,1;0rad)
  Width = 44
FEATURE [Part::Box] Box262  label="Cube221"
  AttacherType = Attacher::AttachEngine3D
  Height = 7
  Length = 10
  Placement = pos=(-15,34.6,-2) rot=(0,0,1;0rad)
  Width = 2
FEATURE [Part::Box] Box263  label="Cube222"
  AttacherType = Attacher::AttachEngine3D
  Height = 7
  Length = 10
  Placement = pos=(-15,25.4,-2) rot=(0,0,1;0rad)
  Width = 2
FEATURE [Part::MultiFuse] Fusion096
  Shapes = -> [Box255,Box258,Box252,Box263,Box262]
FEATURE [Part::Box] Box264  label="Cube223"
  AttacherType = Attacher::AttachEngine3D
  Height = 7
  Length = 4
  Placement = pos=(-6,36.6,-2) rot=(0,0,1;0rad)
  Width = 1
FEATURE [Part::MultiFuse] Fusion095  label="Extra Holes for Clips008"
  Shapes = -> [Box256,Box253,Box264,Box257,Box260,Box259]
FEATURE [Part::Fuse] Fusion098  label="Bumps008"
  Base = -> Sphere079
  Tool = -> Sphere081
FEATURE [Part::Fuse] Fusion094
  Base = -> Fusion098
  Tool = -> Fusion096
FEATURE [Part::Sphere] Sphere082
  Angle1 = -90
  Angle2 = 90
  Angle3 = 360
  AttacherType = Attacher::AttachEngine3D
  Placement = pos=(-7.5,34,0.5) rot=(0,0,1;0rad)
  Radius = 1.5
FEATURE [Part::Fuse] Fusion097  label="Holes008"
  Base = -> Sphere080
  Tool = -> Sphere082
FEATURE [Part::Cut] Cut101
  Base = -> Fusion094
  Tool = -> Fusion097
FEATURE [Part::Cut] Cut097
  Base = -> Cut101
  Tool = -> Fusion095
FEATURE [Part::Cut] Cut098
  Base = -> Cut097
  Tool = -> Box261
FEATURE [Part::Cut] Cut099
  Base = -> Cut098
  Tool = -> Box251
FEATURE [Part::Cut] Cut100  label="Edge Clips006"
  Base = -> Cut099
  Placement = pos=(-20,20,0) rot=(0,0,-1;1.5708rad)
  Tool = -> Box254
FEATURE [Part::Box] Box265  label="Cube224"
  AttacherType = Attacher::AttachEngine3D
  Height = 10
  Length = 10
  Placement = pos=(4,-26,1) rot=(0.205904,-0.974848,-0.085288;0.803573rad)
  Width = 15
FEATURE [Part::Box] Box266  label="Cube225"
  AttacherType = Attacher::AttachEngine3D
  Height = 10
  Length = 10
  Placement = pos=(-26,-4,1) rot=(-0.273007,-0.419215,-0.865867;1.78566rad)
  Width = 15
FEATURE [Part::Box] Box267  label="Cube226"
  AttacherType = Attacher::AttachEngine3D
  Height = 10
  Length = 10
  Placement = pos=(-4,26,1) rot=(0.381439,0.080566,0.920876;3.07487rad)
  Width = 15
FEATURE [Part::Box] Box268  label="Cube227"
  AttacherType = Attacher::AttachEngine3D
  Height = 10
  Length = 10
  Placement = pos=(26,4,1) rot=(0.442189,-0.287968,0.849437;1.66134rad)
  Width = 15
FEATURE [Part::MultiFuse] Fusion099  label="Glue Dents001"
  Shapes = -> [Box265,Box266,Box267,Box268]
FEATURE [Part::MultiFuse] Fusion100  label="Edge Clips Fusion001"
  Shapes = -> [Cut100,Cut086,Cut091,Cut092]
FEATURE [Drawing::FeatureViewAnnotation] Annotation001
  Font = Sans
  Rotation = 0
  Scale = 7
  Text = 0.5 rejigged whole thing, stopped clips overhang and moved bump and holes back 0.5
  ViewResult = <g transform="translate(14,30) rotate(0)">\n<text id="Annotation001"\n font-family="Sans"\n font-size="7"\n fill="#000000">\n<tspan x="0" dy="1em">0.5 rejigged whole thing, stopped clips overhang and moved bump and holes back 0.5</tspan>\n</text>\n</g>
  Visible = false
  X = 14
  Y = 30
FEATURE [Part::Cylinder] Cylinder027
  Angle = 360
  AttacherType = Attacher::AttachEngine3D
  Height = 73
  Placement = pos=(0,0,-50) rot=(0,0,1;0rad)
  Radius = 0.5
FEATURE [Part::MultiFuse] Fusion101
  Placement = pos=(-15,-15,0) rot=(0,0,1;0rad)
  Shapes = -> [Box069,Cylinder018,Sphere030]
FEATURE [App::DocumentObjectGroup] Group002  label="Old 0.1"
  Group = -> [Sphere027,Sphere028,Sphere029,Sphere031,Sphere032,Sphere033,Sphere034,Cylinder012,Cylinder016,Cylinder015,Cylinder014,Cylinder013,Cylinder017,Cylinder019,Box067,Box073,Box071,Box068,Box070,Box072,Box074]
FEATURE [Part::Box] Box269  label="Square Nut Hole 024"
  AttacherType = Attacher::AttachEngine3D
  Height = 2
  Length = 5.8
  Placement = pos=(-2.9,2.9,2.1) rot=(1,0,0;3.14159rad)
  Width = 5.8
FEATURE [Part::Cylinder] Cylinder028
  Angle = 360
  AttacherType = Attacher::AttachEngine3D
  Height = 10
  Placement = pos=(0,0,6.7) rot=(1,0,0;3.14159rad)
  Radius = 1.7
FEATURE [Part::Sphere] Sphere083
  Angle1 = -90
  Angle2 = 90
  Angle3 = 360
  AttacherType = Attacher::AttachEngine3D
  Placement = pos=(0,0,4.3) rot=(1,0,0;3.14159rad)
  Radius = 3.35
FEATURE [Part::MultiFuse] Fusion102
  Placement = pos=(-15,0,0) rot=(0,0,1;0rad)
  Shapes = -> [Box269,Cylinder028,Sphere083]
FEATURE [Part::Fuse] Fusion103
  Base = -> Fusion101
  Tool = -> Fusion102
FEATURE [Part::Feature] Fusion103001
  Placement = pos=(0,0,0) rot=(0,0,1;1.5708rad)
  shape: bbox 21.7 x 6.7 x 10.95 mm, 18 faces, 2 solids (baked)
FEATURE [Part::Feature] Fusion103002
  Placement = pos=(0,0,0) rot=(0,0,1;3.14159rad)
  shape: bbox 6.7 x 21.7 x 10.95 mm, 18 faces, 2 solids (baked)
FEATURE [Part::Feature] Fusion103003
  Placement = pos=(0,0,0) rot=(0,0,-1;1.5708rad)
  shape: bbox 21.7 x 6.7 x 10.95 mm, 18 faces, 2 solids (baked)
FEATURE [Part::MultiFuse] Fusion103004  label="Nut Holes"
  Shapes = -> [Fusion103,Fusion103001,Fusion103002,Fusion103003]
FEATURE [Part::Fuse] Fusion103005  label="Cube with Edge Clips"
  Base = -> Box075
  Tool = -> Fusion100
FEATURE [Part::Cut] Cut102
  Base = -> Fusion103005
  Tool = -> Fusion099
FEATURE [Part::Cut] Cut103
  Base = -> Cut102
  Tool = -> Fusion103004
FEATURE [Part::Cut] Cut104
  Base = -> Cut103
  Tool = -> Chamfer014
FEATURE [Part::Cut] Cut105
  Base = -> Cut104
  Tool = -> Chamfer013
FEATURE [Part::Cut] Cut106  label="Nut Plate 1.0"
  Base = -> Cut105
  Tool = -> Box145
FEATURE [Part::Fuse] Fusion103006
  Base = -> Cut047
  Tool = -> Fusion076
FEATURE [Part::Cut] Cut107
  Base = -> Fusion103006
  Tool = -> Fusion052
FEATURE [Part::Cut] Cut108
  Base = -> Cut107
  Tool = -> Chamfer008
FEATURE [Part::Cut] Cut109
  Base = -> Cut108
  Tool = -> Box085
FEATURE [Part::Cut] Cut110  label="Ball Plate 1.0"
  Base = -> Cut109
  Tool = -> Fusion078
FEATURE [Drawing::FeatureViewAnnotation] Annotation002
  Font = Sans
  Rotation = 0
  Scale = 7
  ViewResult = <g transform="translate(10,10) rotate(0)">\n<text id="Annotation002"\n font-family="Sans"\n font-size="7"\n fill="#000000">\n<tspan x="0" dy="1em"></tspan>\n</text>\n</g>
  Visible = true
  X = 10
  Y = 10
FEATURE [Drawing::FeatureViewAnnotation] Annotation003
  Font = Sans
  Rotation = 0
  Scale = 7
  Text = 0.5 - > 1.0
  ViewResult = <g transform="translate(14,18) rotate(0)">\n<text id="Annotation003"\n font-family="Sans"\n font-size="7"\n fill="#000000">\n<tspan x="0" dy="1em">0.5 - > 1.0</tspan>\n</text>\n</g>
  Visible = false
  X = 14
  Y = 18
FEATURE [Drawing::FeatureViewAnnotation] Annotation004
  Font = Sans
  Rotation = 0
  Scale = 7
  ViewResult = <g transform="translate(10,10) rotate(0)">\n<text id="Annotation004"\n font-family="Sans"\n font-size="7"\n fill="#000000">\n<tspan x="0" dy="1em"></tspan>\n</text>\n</g>
  Visible = true
  X = 10
  Y = 10
FEATURE [Drawing::FeaturePage] Page
  EditableTexts = AUTHOR NAME | CREATION DATE | SUPERVISOR NAME | CHECK DATE | SCALE | WEIGHT | NUMBER | SHEET | TITLE | SUBTITLE
  Group = -> [Annotation,Annotation001,Annotation002,Annotation004]
  Template = <path>
FEATURE [Drawing::FeatureViewAnnotation] Annotation005
  Font = Sans
  Rotation = 0
  Scale = 5
  Text = 0.5 is a working version. 1.0 has everything moved to centre point and then the ball and nut holes moved so that blocks can be mounted in half position
  ViewResult = <g transform="translate(10,30) rotate(0)">\n<text id="Annotation005"\n font-family="Sans"\n font-size="5"\n fill="#000000">\n<tspan x="0" dy="1em">0.5 is a working version. 1.0 has everything moved to centre point and then the ball and nut holes moved so that blocks can be mounted in half position</tspan>\n</text>\n</g>
  Visible = false
  X = 10
  Y = 30
FEATURE [Drawing::FeaturePage] Page001
  EditableTexts = AUTHOR NAME | CREATION DATE | SUPERVISOR NAME | CHECK DATE | SCALE | WEIGHT | NUMBER | SHEET | TITLE | SUBTITLE
  Group = -> [Annotation003,Annotation005]
  Template = <path>
note: 2 file-system paths scrubbed to <path> (originals preserved in the JSON sidecar)
